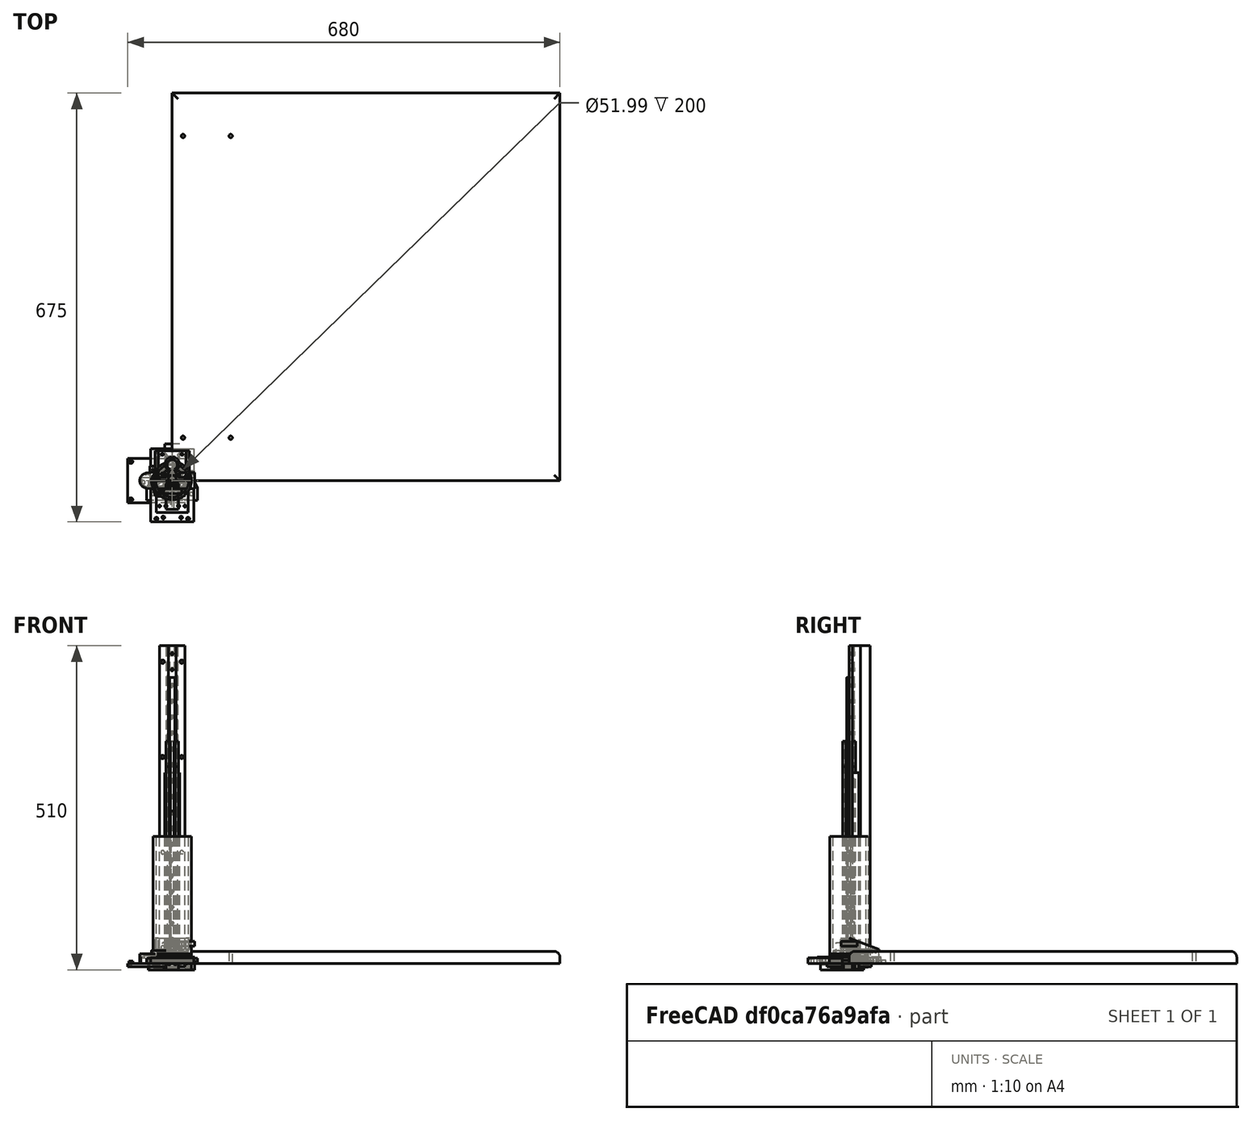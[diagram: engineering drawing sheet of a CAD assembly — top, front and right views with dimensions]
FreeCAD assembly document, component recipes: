
FREECAD ASSEMBLY — COMPONENT RECIPES ("MUSCLE_ROLLER_1V0")

This assembly document has 39 components, labeled P0..P38 below (a component is one placed body or linked part). 39 of them carry a construction recipe — the FreeCAD feature program that regenerates the part from scratch, quoted from this document or its linked companion documents; the rest are supplied as boundary geometry only. No exploded tour is included for this assembly.
NOTE — this tour is split across 2 documents so each fits a 32k-token context. This is document 1: the component sections continue in the remaining 1 document, each repeating the header above.
COMPONENT P0 — recipe-attached ("BAR_A_1V0", modeled in this document).
Construction recipe (the document's own serialized feature program — sketch geometry with constraints, then the solid features built on it; lengths are millimeters unless a unit is written):

FEATURE [Sketcher::SketchObject] Sketch100
  FullyConstrained = true
  MapMode = 5
  Support = -> [XY_Plane080]
  sketch-geometry (57):
    g0: LineSegment StartX=-10 StartY=10 StartZ=0 EndX=10 EndY=10 EndZ=0
    g1: LineSegment StartX=10 StartY=10 StartZ=0 EndX=10 EndY=-10 EndZ=0
    g2: LineSegment StartX=10 StartY=-10 StartZ=0 EndX=-10 EndY=-10 EndZ=0
    g3: LineSegment StartX=-10 StartY=-10 StartZ=0 EndX=-10 EndY=10 EndZ=0
    g4: LineSegment StartX=-3.9 StartY=-3.9 StartZ=0 EndX=3.9 EndY=-3.9 EndZ=0
    g5: LineSegment StartX=3.9 StartY=-3.9 StartZ=0 EndX=3.9 EndY=3.9 EndZ=0
    g6: LineSegment StartX=3.9 StartY=3.9 StartZ=0 EndX=-3.9 EndY=3.9 EndZ=0
    g7: LineSegment StartX=-3.9 StartY=3.9 StartZ=0 EndX=-3.9 EndY=-3.9 EndZ=0
    g8: LineSegment StartX=-8.2 StartY=8.2 StartZ=0 EndX=8.2 EndY=8.2 EndZ=0
    g9: LineSegment StartX=8.2 StartY=8.2 StartZ=0 EndX=8.2 EndY=-8.2 EndZ=0
    g10: LineSegment StartX=8.2 StartY=-8.2 StartZ=0 EndX=-8.2 EndY=-8.2 EndZ=0
    g11: LineSegment StartX=-8.2 StartY=-8.2 StartZ=0 EndX=-8.2 EndY=8.2 EndZ=0
    g12: Circle CenterX=0 CenterY=0 CenterZ=0 NormalX=0 NormalY=0 NormalZ=1 AngleXU=0 Radius=2.1
    g13: LineSegment StartX=-10 StartY=-10 StartZ=0 EndX=-10 EndY=-4.9 EndZ=0
    g14: LineSegment StartX=-10 StartY=-4.9 StartZ=0 EndX=-8.2 EndY=-3.1 EndZ=0
    g15: LineSegment StartX=-8.2 StartY=-3.1 StartZ=0 EndX=-8.2 EndY=-5.5 EndZ=0
    g16: LineSegment StartX=-6.56066 StartY=-5.5 StartZ=0 EndX=-3.9 EndY=-2.83934 EndZ=0
    g17: LineSegment StartX=-3.9 StartY=-2.83934 StartZ=0 EndX=-3.9 EndY=2.83934 EndZ=0
    g18: LineSegment StartX=-3.9 StartY=2.83934 StartZ=0 EndX=-6.56066 EndY=5.5 EndZ=0
    g19: LineSegment StartX=-8.2 StartY=5.5 StartZ=0 EndX=-8.2 EndY=3.1 EndZ=0
    g20: LineSegment StartX=-8.2 StartY=3.1 StartZ=0 EndX=-10 EndY=4.9 EndZ=0
    g21: LineSegment StartX=-10 StartY=4.9 StartZ=0 EndX=-10 EndY=10 EndZ=0
    g22: LineSegment StartX=-10 StartY=10 StartZ=0 EndX=-4.9 EndY=10 EndZ=0
    g23: LineSegment StartX=-4.9 StartY=10 StartZ=0 EndX=-3.1 EndY=8.2 EndZ=0
    g24: LineSegment StartX=-3.1 StartY=8.2 StartZ=0 EndX=-5.5 EndY=8.2 EndZ=0
    g25: LineSegment StartX=-5.5 StartY=6.56066 StartZ=0 EndX=-2.83934 EndY=3.9 EndZ=0
    g26: LineSegment StartX=-2.83934 StartY=3.9 StartZ=0 EndX=2.83934 EndY=3.9 EndZ=0
    g27: LineSegment StartX=2.83934 StartY=3.9 StartZ=0 EndX=5.5 EndY=6.56066 EndZ=0
    g28: LineSegment StartX=5.5 StartY=8.2 StartZ=0 EndX=3.1 EndY=8.2 EndZ=0
    g29: LineSegment StartX=3.1 StartY=8.2 StartZ=0 EndX=4.9 EndY=10 EndZ=0
    g30: LineSegment StartX=4.9 StartY=10 StartZ=0 EndX=10 EndY=10 EndZ=0
    g31: LineSegment StartX=10 StartY=10 StartZ=0 EndX=10 EndY=4.9 EndZ=0
    g32: LineSegment StartX=10 StartY=4.9 StartZ=0 EndX=8.2 EndY=3.1 EndZ=0
    g33: LineSegment StartX=8.2 StartY=3.1 StartZ=0 EndX=8.2 EndY=5.5 EndZ=0
    g34: LineSegment StartX=6.56066 StartY=5.5 StartZ=0 EndX=3.9 EndY=2.83934 EndZ=0
    g35: LineSegment StartX=3.9 StartY=2.83934 StartZ=0 EndX=3.9 EndY=-2.83934 EndZ=0
    g36: LineSegment StartX=3.9 StartY=-2.83934 StartZ=0 EndX=6.56066 EndY=-5.5 EndZ=0
    g37: LineSegment StartX=8.2 StartY=-5.5 StartZ=0 EndX=8.2 EndY=-3.1 EndZ=0
    g38: LineSegment StartX=8.2 StartY=-3.1 StartZ=0 EndX=10 EndY=-4.9 EndZ=0
    g39: LineSegment StartX=10 StartY=-4.9 StartZ=0 EndX=10 EndY=-10 EndZ=0
    g40: LineSegment StartX=10 StartY=-10 StartZ=0 EndX=4.9 EndY=-10 EndZ=0
    g41: LineSegment StartX=4.9 StartY=-10 StartZ=0 EndX=3.1 EndY=-8.2 EndZ=0
    g42: LineSegment StartX=3.1 StartY=-8.2 StartZ=0 EndX=5.5 EndY=-8.2 EndZ=0
    g43: LineSegment StartX=5.5 StartY=-6.56066 StartZ=0 EndX=2.83934 EndY=-3.9 EndZ=0
    g44: LineSegment StartX=2.83934 StartY=-3.9 StartZ=0 EndX=-2.83934 EndY=-3.9 EndZ=0
    g45: LineSegment StartX=-2.83934 StartY=-3.9 StartZ=0 EndX=-5.5 EndY=-6.56066 EndZ=0
    g46: LineSegment StartX=-5.5 StartY=-8.2 StartZ=0 EndX=-3.1 EndY=-8.2 EndZ=0
    g47: LineSegment StartX=-3.1 StartY=-8.2 StartZ=0 EndX=-4.9 EndY=-10 EndZ=0
    g48: LineSegment StartX=-4.9 StartY=-10 StartZ=0 EndX=-10 EndY=-10 EndZ=0
    g49: LineSegment StartX=-5.5 StartY=-8.2 StartZ=0 EndX=-5.5 EndY=-6.56066 EndZ=0
    g50: LineSegment StartX=-6.56066 StartY=-5.5 StartZ=0 EndX=-8.2 EndY=-5.5 EndZ=0
    g51: LineSegment StartX=-8.2 StartY=5.5 StartZ=0 EndX=-6.56066 EndY=5.5 EndZ=0
    g52: LineSegment StartX=-5.5 StartY=6.56066 StartZ=0 EndX=-5.5 EndY=8.2 EndZ=0
    g53: LineSegment StartX=5.5 StartY=8.2 StartZ=0 EndX=5.5 EndY=6.56066 EndZ=0
    g54: LineSegment StartX=6.56066 StartY=5.5 StartZ=0 EndX=8.2 EndY=5.5 EndZ=0
    g55: LineSegment StartX=6.56066 StartY=-5.5 StartZ=0 EndX=8.2 EndY=-5.5 EndZ=0
    g56: LineSegment StartX=5.5 StartY=-6.56066 StartZ=0 EndX=5.5 EndY=-8.2 EndZ=0
  constraints (133):
    c: Coincident(g0,g1)
    c: Coincident(g1,g2)
    c: Coincident(g2,g3)
    c: Coincident(g3,g0)
    c: Horizontal(g2)
    c: Vertical(g1)
    c: Equal(g3,g0)
    c: Symmetric(g0,g2,g-1)
    c: Symmetric(g0,g0,g-2)
    c: DistanceX(g0,g0) = 20
    c: Coincident(g4,g5)
    c: Coincident(g5,g6)
    c: Coincident(g6,g7)
    c: Coincident(g7,g4)
    c: Horizontal(g6)
    c: Vertical(g7)
    c: DistanceX(g2,g4) = 6.1
    c: DistanceY(g2,g4) = 6.1
    c: Coincident(g8,g9)
    c: Coincident(g9,g10)
    c: Coincident(g10,g11)
    c: Coincident(g11,g8)
    c: Horizontal(g8)
    c: Vertical(g11)
    c: DistanceX(g2,g10) = 1.8
    c: DistanceY(g2,g10) = 1.8
    c: Symmetric(g10,g9,g-2)
    c: Symmetric(g4,g4,g-2)
    c: Symmetric(g5,g4,g-1)
    c: Symmetric(g8,g9,g-1)
    c: Coincident(g12,g-1)
    c: Diameter(g12) = 4.2
    c: Coincident(g2,g13)
    c: PointOnObject(g13,g3)
    c: Coincident(g13,g14)
    c: PointOnObject(g14,g11)
    c: Coincident(g14,g15)
    c: PointOnObject(g16,g7)
    c: Coincident(g16,g17)
    c: Coincident(g17,g18)
    c: Coincident(g19,g20)
    c: Coincident(g20,g21)
    c: Coincident(g21,g0)
    c: Coincident(g21,g22)
    c: PointOnObject(g22,g0)
    c: Coincident(g22,g23)
    c: PointOnObject(g23,g8)
    c: Coincident(g23,g24)
    c: PointOnObject(g25,g6)
    c: Coincident(g25,g26)
    c: Coincident(g26,g27)
    c: Coincident(g28,g29)
    c: Coincident(g29,g30)
    c: Coincident(g30,g0)
    c: Coincident(g30,g31)
    c: Coincident(g31,g32)
    c: Coincident(g32,g33)
    c: Coincident(g34,g35)
    c: Coincident(g35,g36)
    c: Coincident(g37,g38)
    c: Coincident(g38,g39)
    c: Coincident(g39,g1)
    c: Coincident(g39,g40)
    c: PointOnObject(g40,g2)
    c: Coincident(g40,g41)
    c: Coincident(g41,g42)
    c: PointOnObject(g43,g4)
    c: Coincident(g43,g44)
    c: Coincident(g44,g45)
    c: Coincident(g46,g47)
    c: Coincident(g47,g48)
    c: Coincident(g48,g13)
    c: Angle(g2,g47) = 0.785398
    c: Parallel(g47,g45)
    c: Parallel(g45,g16)
    c: Parallel(g16,g14)
    c: DistanceY(g14,g19) = 6.2
    c: Symmetric(g19,g14,g-1)
    c: Equal(g48,g13)
    c: Coincident(g16,g50)
    c: Coincident(g15,g50)
    c: Coincident(g46,g49)
    c: Coincident(g45,g49)
    c: Vertical(g49)
    c: Horizontal(g50)
    c: Vertical(g52)
    c: Coincident(g24,g52)
    c: Coincident(g25,g52)
    c: Coincident(g18,g51)
    c: Coincident(g19,g51)
    c: DistanceY(g15,g19) = 11
    c: Symmetric(g20,g13,g-1)
    c: Equal(g50,g49)
    c: Equal(g46,g15)
    c: Horizontal(g46)
    c: Distance(g45,g16) = 1.5
    c: Symmetric(g15,g19,g-1)
    c: Equal(g22,g21)
    c: Symmetric(g23,g46,g-1)
    c: Symmetric(g25,g45,g-1)
    c: Symmetric(g18,g16,g-1)
    c: Symmetric(g17,g16,g-1)
    c: Symmetric(g25,g44,g-1)
    c: Symmetric(g23,g28,g-2)
    c: Symmetric(g29,g22,g-2)
    c: Symmetric(g26,g25,g-2)
    c: Coincident(g28,g53)
    c: Coincident(g27,g53)
    c: Coincident(g34,g54)
    c: Coincident(g33,g54)
    c: Symmetric(g28,g24,g-2)
    c: Symmetric(g27,g25,g-2)
    c: Symmetric(g34,g18,g-2)
    c: Symmetric(g33,g19,g-2)
    c: Symmetric(g34,g17,g-2)
    c: Horizontal(g28)
    c: Symmetric(g32,g37,g-1)
    c: Symmetric(g31,g38,g-1)
    c: Symmetric(g32,g19,g-2)
    c: Symmetric(g31,g20,g-2)
    c: Coincident(g36,g55)
    c: Coincident(g37,g55)
    c: Coincident(g42,g56)
    c: Coincident(g43,g56)
    c: Symmetric(g36,g34,g-1)
    c: Symmetric(g37,g33,g-1)
    c: Symmetric(g43,g45,g-2)
    c: Symmetric(g35,g34,g-1)
    c: Symmetric(g42,g46,g-2)
    c: Symmetric(g41,g46,g-2)
    c: Symmetric(g40,g47,g-2)
    c: Vertical(g37)
    c: Parallel(g43,g36)
FEATURE [PartDesign::Pad] Pad063
  Direction = (1,1,1)
  Length = 350
  Length2 = 100
  Profile = -> Sketch100
  Type = 0
FEATURE [PartDesign::Body] Body007
  Group = -> [Sketch100,Pad063]
  Origin = -> Origin079
  Tip = -> Pad063
COMPONENT P1 — recipe-attached ("BAR_B_1V0", modeled in this document).
Construction recipe (the document's own serialized feature program — sketch geometry with constraints, then the solid features built on it; lengths are millimeters unless a unit is written):

FEATURE [Sketcher::SketchObject] Sketch105
  FullyConstrained = true
  MapMode = 5
  Support = -> [XY_Plane086]
  sketch-geometry (57):
    g0: LineSegment StartX=-10 StartY=10 StartZ=0 EndX=10 EndY=10 EndZ=0
    g1: LineSegment StartX=10 StartY=10 StartZ=0 EndX=10 EndY=-10 EndZ=0
    g2: LineSegment StartX=10 StartY=-10 StartZ=0 EndX=-10 EndY=-10 EndZ=0
    g3: LineSegment StartX=-10 StartY=-10 StartZ=0 EndX=-10 EndY=10 EndZ=0
    g4: LineSegment StartX=-3.9 StartY=-3.9 StartZ=0 EndX=3.9 EndY=-3.9 EndZ=0
    g5: LineSegment StartX=3.9 StartY=-3.9 StartZ=0 EndX=3.9 EndY=3.9 EndZ=0
    g6: LineSegment StartX=3.9 StartY=3.9 StartZ=0 EndX=-3.9 EndY=3.9 EndZ=0
    g7: LineSegment StartX=-3.9 StartY=3.9 StartZ=0 EndX=-3.9 EndY=-3.9 EndZ=0
    g8: LineSegment StartX=-8.2 StartY=8.2 StartZ=0 EndX=8.2 EndY=8.2 EndZ=0
    g9: LineSegment StartX=8.2 StartY=8.2 StartZ=0 EndX=8.2 EndY=-8.2 EndZ=0
    g10: LineSegment StartX=8.2 StartY=-8.2 StartZ=0 EndX=-8.2 EndY=-8.2 EndZ=0
    g11: LineSegment StartX=-8.2 StartY=-8.2 StartZ=0 EndX=-8.2 EndY=8.2 EndZ=0
    g12: Circle CenterX=0 CenterY=0 CenterZ=0 NormalX=0 NormalY=0 NormalZ=1 AngleXU=0 Radius=2.1
    g13: LineSegment StartX=-10 StartY=-10 StartZ=0 EndX=-10 EndY=-4.9 EndZ=0
    g14: LineSegment StartX=-10 StartY=-4.9 StartZ=0 EndX=-8.2 EndY=-3.1 EndZ=0
    g15: LineSegment StartX=-8.2 StartY=-3.1 StartZ=0 EndX=-8.2 EndY=-5.5 EndZ=0
    g16: LineSegment StartX=-6.56066 StartY=-5.5 StartZ=0 EndX=-3.9 EndY=-2.83934 EndZ=0
    g17: LineSegment StartX=-3.9 StartY=-2.83934 StartZ=0 EndX=-3.9 EndY=2.83934 EndZ=0
    g18: LineSegment StartX=-3.9 StartY=2.83934 StartZ=0 EndX=-6.56066 EndY=5.5 EndZ=0
    g19: LineSegment StartX=-8.2 StartY=5.5 StartZ=0 EndX=-8.2 EndY=3.1 EndZ=0
    g20: LineSegment StartX=-8.2 StartY=3.1 StartZ=0 EndX=-10 EndY=4.9 EndZ=0
    g21: LineSegment StartX=-10 StartY=4.9 StartZ=0 EndX=-10 EndY=10 EndZ=0
    g22: LineSegment StartX=-10 StartY=10 StartZ=0 EndX=-4.9 EndY=10 EndZ=0
    g23: LineSegment StartX=-4.9 StartY=10 StartZ=0 EndX=-3.1 EndY=8.2 EndZ=0
    g24: LineSegment StartX=-3.1 StartY=8.2 StartZ=0 EndX=-5.5 EndY=8.2 EndZ=0
    g25: LineSegment StartX=-5.5 StartY=6.56066 StartZ=0 EndX=-2.83934 EndY=3.9 EndZ=0
    g26: LineSegment StartX=-2.83934 StartY=3.9 StartZ=0 EndX=2.83934 EndY=3.9 EndZ=0
    g27: LineSegment StartX=2.83934 StartY=3.9 StartZ=0 EndX=5.5 EndY=6.56066 EndZ=0
    g28: LineSegment StartX=5.5 StartY=8.2 StartZ=0 EndX=3.1 EndY=8.2 EndZ=0
    g29: LineSegment StartX=3.1 StartY=8.2 StartZ=0 EndX=4.9 EndY=10 EndZ=0
    g30: LineSegment StartX=4.9 StartY=10 StartZ=0 EndX=10 EndY=10 EndZ=0
    g31: LineSegment StartX=10 StartY=10 StartZ=0 EndX=10 EndY=4.9 EndZ=0
    g32: LineSegment StartX=10 StartY=4.9 StartZ=0 EndX=8.2 EndY=3.1 EndZ=0
    g33: LineSegment StartX=8.2 StartY=3.1 StartZ=0 EndX=8.2 EndY=5.5 EndZ=0
    g34: LineSegment StartX=6.56066 StartY=5.5 StartZ=0 EndX=3.9 EndY=2.83934 EndZ=0
    g35: LineSegment StartX=3.9 StartY=2.83934 StartZ=0 EndX=3.9 EndY=-2.83934 EndZ=0
    g36: LineSegment StartX=3.9 StartY=-2.83934 StartZ=0 EndX=6.56066 EndY=-5.5 EndZ=0
    g37: LineSegment StartX=8.2 StartY=-5.5 StartZ=0 EndX=8.2 EndY=-3.1 EndZ=0
    g38: LineSegment StartX=8.2 StartY=-3.1 StartZ=0 EndX=10 EndY=-4.9 EndZ=0
    g39: LineSegment StartX=10 StartY=-4.9 StartZ=0 EndX=10 EndY=-10 EndZ=0
    g40: LineSegment StartX=10 StartY=-10 StartZ=0 EndX=4.9 EndY=-10 EndZ=0
    g41: LineSegment StartX=4.9 StartY=-10 StartZ=0 EndX=3.1 EndY=-8.2 EndZ=0
    g42: LineSegment StartX=3.1 StartY=-8.2 StartZ=0 EndX=5.5 EndY=-8.2 EndZ=0
    g43: LineSegment StartX=5.5 StartY=-6.56066 StartZ=0 EndX=2.83934 EndY=-3.9 EndZ=0
    g44: LineSegment StartX=2.83934 StartY=-3.9 StartZ=0 EndX=-2.83934 EndY=-3.9 EndZ=0
    g45: LineSegment StartX=-2.83934 StartY=-3.9 StartZ=0 EndX=-5.5 EndY=-6.56066 EndZ=0
    g46: LineSegment StartX=-5.5 StartY=-8.2 StartZ=0 EndX=-3.1 EndY=-8.2 EndZ=0
    g47: LineSegment StartX=-3.1 StartY=-8.2 StartZ=0 EndX=-4.9 EndY=-10 EndZ=0
    g48: LineSegment StartX=-4.9 StartY=-10 StartZ=0 EndX=-10 EndY=-10 EndZ=0
    g49: LineSegment StartX=-5.5 StartY=-8.2 StartZ=0 EndX=-5.5 EndY=-6.56066 EndZ=0
    g50: LineSegment StartX=-6.56066 StartY=-5.5 StartZ=0 EndX=-8.2 EndY=-5.5 EndZ=0
    g51: LineSegment StartX=-8.2 StartY=5.5 StartZ=0 EndX=-6.56066 EndY=5.5 EndZ=0
    g52: LineSegment StartX=-5.5 StartY=6.56066 StartZ=0 EndX=-5.5 EndY=8.2 EndZ=0
    g53: LineSegment StartX=5.5 StartY=8.2 StartZ=0 EndX=5.5 EndY=6.56066 EndZ=0
    g54: LineSegment StartX=6.56066 StartY=5.5 StartZ=0 EndX=8.2 EndY=5.5 EndZ=0
    g55: LineSegment StartX=6.56066 StartY=-5.5 StartZ=0 EndX=8.2 EndY=-5.5 EndZ=0
    g56: LineSegment StartX=5.5 StartY=-6.56066 StartZ=0 EndX=5.5 EndY=-8.2 EndZ=0
  constraints (133):
    c: Coincident(g0,g1)
    c: Coincident(g1,g2)
    c: Coincident(g2,g3)
    c: Coincident(g3,g0)
    c: Horizontal(g2)
    c: Vertical(g1)
    c: Equal(g3,g0)
    c: Symmetric(g0,g2,g-1)
    c: Symmetric(g0,g0,g-2)
    c: DistanceX(g0,g0) = 20
    c: Coincident(g4,g5)
    c: Coincident(g5,g6)
    c: Coincident(g6,g7)
    c: Coincident(g7,g4)
    c: Horizontal(g6)
    c: Vertical(g7)
    c: DistanceX(g2,g4) = 6.1
    c: DistanceY(g2,g4) = 6.1
    c: Coincident(g8,g9)
    c: Coincident(g9,g10)
    c: Coincident(g10,g11)
    c: Coincident(g11,g8)
    c: Horizontal(g8)
    c: Vertical(g11)
    c: DistanceX(g2,g10) = 1.8
    c: DistanceY(g2,g10) = 1.8
    c: Symmetric(g10,g9,g-2)
    c: Symmetric(g4,g4,g-2)
    c: Symmetric(g5,g4,g-1)
    c: Symmetric(g8,g9,g-1)
    c: Coincident(g12,g-1)
    c: Diameter(g12) = 4.2
    c: Coincident(g2,g13)
    c: PointOnObject(g13,g3)
    c: Coincident(g13,g14)
    c: PointOnObject(g14,g11)
    c: Coincident(g14,g15)
    c: PointOnObject(g16,g7)
    c: Coincident(g16,g17)
    c: Coincident(g17,g18)
    c: Coincident(g19,g20)
    c: Coincident(g20,g21)
    c: Coincident(g21,g0)
    c: Coincident(g21,g22)
    c: PointOnObject(g22,g0)
    c: Coincident(g22,g23)
    c: PointOnObject(g23,g8)
    c: Coincident(g23,g24)
    c: PointOnObject(g25,g6)
    c: Coincident(g25,g26)
    c: Coincident(g26,g27)
    c: Coincident(g28,g29)
    c: Coincident(g29,g30)
    c: Coincident(g30,g0)
    c: Coincident(g30,g31)
    c: Coincident(g31,g32)
    c: Coincident(g32,g33)
    c: Coincident(g34,g35)
    c: Coincident(g35,g36)
    c: Coincident(g37,g38)
    c: Coincident(g38,g39)
    c: Coincident(g39,g1)
    c: Coincident(g39,g40)
    c: PointOnObject(g40,g2)
    c: Coincident(g40,g41)
    c: Coincident(g41,g42)
    c: PointOnObject(g43,g4)
    c: Coincident(g43,g44)
    c: Coincident(g44,g45)
    c: Coincident(g46,g47)
    c: Coincident(g47,g48)
    c: Coincident(g48,g13)
    c: Angle(g2,g47) = 0.785398
    c: Parallel(g47,g45)
    c: Parallel(g45,g16)
    c: Parallel(g16,g14)
    c: DistanceY(g14,g19) = 6.2
    c: Symmetric(g19,g14,g-1)
    c: Equal(g48,g13)
    c: Coincident(g16,g50)
    c: Coincident(g15,g50)
    c: Coincident(g46,g49)
    c: Coincident(g45,g49)
    c: Vertical(g49)
    c: Horizontal(g50)
    c: Vertical(g52)
    c: Coincident(g24,g52)
    c: Coincident(g25,g52)
    c: Coincident(g18,g51)
    c: Coincident(g19,g51)
    c: DistanceY(g15,g19) = 11
    c: Symmetric(g20,g13,g-1)
    c: Equal(g50,g49)
    c: Equal(g46,g15)
    c: Horizontal(g46)
    c: Distance(g45,g16) = 1.5
    c: Symmetric(g15,g19,g-1)
    c: Equal(g22,g21)
    c: Symmetric(g23,g46,g-1)
    c: Symmetric(g25,g45,g-1)
    c: Symmetric(g18,g16,g-1)
    c: Symmetric(g17,g16,g-1)
    c: Symmetric(g25,g44,g-1)
    c: Symmetric(g23,g28,g-2)
    c: Symmetric(g29,g22,g-2)
    c: Symmetric(g26,g25,g-2)
    c: Coincident(g28,g53)
    c: Coincident(g27,g53)
    c: Coincident(g34,g54)
    c: Coincident(g33,g54)
    c: Symmetric(g28,g24,g-2)
    c: Symmetric(g27,g25,g-2)
    c: Symmetric(g34,g18,g-2)
    c: Symmetric(g33,g19,g-2)
    c: Symmetric(g34,g17,g-2)
    c: Horizontal(g28)
    c: Symmetric(g32,g37,g-1)
    c: Symmetric(g31,g38,g-1)
    c: Symmetric(g32,g19,g-2)
    c: Symmetric(g31,g20,g-2)
    c: Coincident(g36,g55)
    c: Coincident(g37,g55)
    c: Coincident(g42,g56)
    c: Coincident(g43,g56)
    c: Symmetric(g36,g34,g-1)
    c: Symmetric(g37,g33,g-1)
    c: Symmetric(g43,g45,g-2)
    c: Symmetric(g35,g34,g-1)
    c: Symmetric(g42,g46,g-2)
    c: Symmetric(g41,g46,g-2)
    c: Symmetric(g40,g47,g-2)
    c: Vertical(g37)
    c: Parallel(g43,g36)
FEATURE [PartDesign::Pad] Pad066
  Direction = (1,1,1)
  Length = 310
  Length2 = 100
  Profile = -> Sketch105
  Type = 0
FEATURE [PartDesign::Body] Body008
  Group = -> [Sketch105,Pad066]
  Origin = -> Origin086
  Tip = -> Pad066
COMPONENT P2 — recipe-attached ("BASE_1V0", modeled in this document).
Construction recipe (the document's own serialized feature program — sketch geometry with constraints, then the solid features built on it; lengths are millimeters unless a unit is written):

FEATURE [PartDesign::CoordinateSystem] LCS_0064
  AttacherType = Attacher::AttachEngine3D
  MapMode = 2
  Support = -> [X_Axis070]
FEATURE [Sketcher::SketchObject] Sketch086
  FullyConstrained = true
  MapMode = 5
  Support = -> [XY_Plane070]
  sketch-geometry (10):
    g0: LineSegment StartX=0 StartY=0 StartZ=0 EndX=610 EndY=0 EndZ=0
    g1: LineSegment StartX=610 StartY=0 StartZ=0 EndX=610 EndY=610 EndZ=0
    g2: LineSegment StartX=610 StartY=610 StartZ=0 EndX=0 EndY=610 EndZ=0
    g3: LineSegment StartX=0 StartY=610 StartZ=0 EndX=0 EndY=0 EndZ=0
    g4: Circle CenterX=17 CenterY=67.5 CenterZ=0 NormalX=0 NormalY=0 NormalZ=1 AngleXU=0 Radius=2.75
    g5: Circle CenterX=92 CenterY=67.5 CenterZ=0 NormalX=0 NormalY=0 NormalZ=1 AngleXU=0 Radius=2.75
    g6: Circle CenterX=17 CenterY=542.5 CenterZ=0 NormalX=0 NormalY=0 NormalZ=1 AngleXU=0 Radius=2.75
    g7: Circle CenterX=92 CenterY=542.5 CenterZ=0 NormalX=0 NormalY=0 NormalZ=1 AngleXU=0 Radius=2.75
    g8: LineSegment StartX=17 StartY=542.5 StartZ=0 EndX=17 EndY=610 EndZ=0
    g9: LineSegment StartX=17 StartY=67.5 StartZ=0 EndX=17 EndY=0 EndZ=0
  constraints (29):
    c: Coincident(g0,g1)
    c: Coincident(g1,g2)
    c: Coincident(g2,g3)
    c: Coincident(g3,g0)
    c: Horizontal(g0)
    c: Horizontal(g2)
    c: Vertical(g1)
    c: Vertical(g3)
    c: DistanceX(g2,g2) = 610
    c: Coincident(g0,g-1)
    c: DistanceY(g3,g3) = 610
    c: Diameter(g6) = 5.5
    c: Equal(g6,g4)
    c: Equal(g6,g7)
    c: Equal(g6,g5)
    c: Horizontal(g4,g5)
    c: DistanceX(g4,g5) = 75
    c: DistanceX(g-1,g4) = 17
    c: Vertical(g5,g7)
    c: Horizontal(g7,g6)
    c: Vertical(g6,g4)
    c: Coincident(g8,g6)
    c: PointOnObject(g8,g2)
    c: Vertical(g8)
    c: Coincident(g9,g4)
    c: PointOnObject(g9,g0)
    c: Vertical(g9)
    c: Equal(g9,g8)
    c: DistanceY(g4,g6) = 475
FEATURE [PartDesign::Pad] Pad056
  Direction = (1,1,1)
  Length = 19
  Length2 = 100
  Profile = -> Sketch086
  Type = 0
FEATURE [PartDesign::Fillet] Fillet001
  Base = -> Pad056 [Edge4,Edge12,Edge10,Edge7]
  BaseFeature = -> Pad056
  Radius = 9
  SupportTransform = false
FEATURE [PartDesign::Body] Body_9
  Group = -> [LCS_0064,Sketch086,Pad056,Fillet001]
  Origin = -> Origin070
  Tip = -> Fillet001
COMPONENT P3 — recipe-attached ("BEARING_X_1V0", modeled in this document).
Construction recipe (the document's own serialized feature program — sketch geometry with constraints, then the solid features built on it; lengths are millimeters unless a unit is written):

FEATURE [PartDesign::CoordinateSystem] LCS_0092
  AttacherType = Attacher::AttachEngine3D
  MapMode = 2
  Support = -> [X_Axis100]
FEATURE [Sketcher::SketchObject] Sketch121
  FullyConstrained = true
  MapMode = 5
  Support = -> [XY_Plane100]
  sketch-geometry (9):
    g0: LineSegment StartX=-7 StartY=11 StartZ=0 EndX=-7 EndY=5 EndZ=0
    g1: LineSegment StartX=-7 StartY=5 StartZ=0 EndX=-17 EndY=5 EndZ=0
    g2: LineSegment StartX=-17 StartY=5 StartZ=0 EndX=-17 EndY=0 EndZ=0
    g3: LineSegment StartX=-17 StartY=0 StartZ=0 EndX=17 EndY=0 EndZ=0
    g4: LineSegment StartX=17 StartY=0 StartZ=0 EndX=17 EndY=5 EndZ=0
    g5: LineSegment StartX=17 StartY=5 StartZ=0 EndX=7 EndY=5 EndZ=0
    g6: LineSegment StartX=7 StartY=5 StartZ=0 EndX=7 EndY=11 EndZ=0
    g7: ArcOfCircle CenterX=0 CenterY=11 CenterZ=0 NormalX=0 NormalY=0 NormalZ=1 AngleXU=0 Radius=7 StartAngle=0 EndAngle=3.14159
    g8: Circle CenterX=0 CenterY=11 CenterZ=0 NormalX=0 NormalY=0 NormalZ=1 AngleXU=0 Radius=4.25
  constraints (27):
    c: Coincident(g0,g1)
    c: Horizontal(g1)
    c: Coincident(g1,g2)
    c: PointOnObject(g2,g-1)
    c: Vertical(g2)
    c: Coincident(g2,g3)
    c: PointOnObject(g3,g-1)
    c: Coincident(g3,g4)
    c: Coincident(g4,g5)
    c: Coincident(g5,g6)
    c: Vertical(g6)
    c: PointOnObject(g7,g-2)
    c: Coincident(g7,g0)
    c: Coincident(g7,g6)
    c: Horizontal(g5)
    c: DistanceY(g2,g2) = 5
    c: Coincident(g8,g7)
    c: Diameter(g8) = 8.5
    c: Diameter(g7) = 14
    c: Horizontal(g0,g7)
    c: Horizontal(g7,g6)
    c: Vertical(g0)
    c: Vertical(g4)
    c: Equal(g4,g2)
    c: DistanceX(g1,g1) = 10
    c: Equal(g5,g1)
    c: DistanceY(g-1,g7) = 11
FEATURE [PartDesign::Pad] Pad074
  Direction = (1,1,1)
  Length = 20
  Length2 = 100
  Midplane = true
  Profile = -> Sketch121
  Refine = true
  Type = 0
FEATURE [Sketcher::SketchObject] Sketch122
  FullyConstrained = true
  MapMode = 5
  Placement = pos=(0,0,0) rot=(1,0,0;1.5708rad)
  Support = -> [XZ_Plane099]
  sketch-geometry (2):
    g0: Circle CenterX=-12 CenterY=0 CenterZ=0 NormalX=0 NormalY=0 NormalZ=1 AngleXU=0 Radius=2.75
    g1: Circle CenterX=12 CenterY=0 CenterZ=0 NormalX=0 NormalY=0 NormalZ=1 AngleXU=0 Radius=2.75
  constraints (5):
    c: PointOnObject(g0,g-1)
    c: Diameter(g1) = 5.5
    c: Equal(g1,g0)
    c: Symmetric(g0,g1,g-2)
    c: DistanceX(g0,g1) = 24
FEATURE [PartDesign::Pocket] Pocket039
  BaseFeature = -> Pad074
  Length = 5
  Length2 = 100
  Profile = -> Sketch122
  Refine = true
  Type = 1
FEATURE [PartDesign::Body] Body_17
  Group = -> [LCS_0092,Sketch121,Pad074,Sketch122,Pocket039]
  Origin = -> Origin100
  Tip = -> Pocket039
COMPONENT P4 — recipe-attached ("CABLE_CARRIER", modeled in this document).
Construction recipe (the document's own serialized feature program — sketch geometry with constraints, then the solid features built on it; lengths are millimeters unless a unit is written):

FEATURE [PartDesign::CoordinateSystem] LCS_0120
  AttacherType = Attacher::AttachEngine3D
  MapMode = 2
  Support = -> [X_Axis130]
FEATURE [Sketcher::SketchObject] Sketch152
  FullyConstrained = true
  MapMode = 5
  Support = -> [XY_Plane130]
  sketch-geometry (4):
    g0: LineSegment StartX=-11.5 StartY=0 StartZ=0 EndX=11.5 EndY=0 EndZ=0
    g1: LineSegment StartX=11.5 StartY=0 StartZ=0 EndX=11.5 EndY=15 EndZ=0
    g2: LineSegment StartX=11.5 StartY=15 StartZ=0 EndX=-11.5 EndY=15 EndZ=0
    g3: LineSegment StartX=-11.5 StartY=15 StartZ=0 EndX=-11.5 EndY=0 EndZ=0
  constraints (11):
    c: Coincident(g0,g1)
    c: Coincident(g1,g2)
    c: Coincident(g2,g3)
    c: Coincident(g3,g0)
    c: Horizontal(g0)
    c: Vertical(g1)
    c: Vertical(g3)
    c: PointOnObject(g0,g-1)
    c: DistanceY(g1,g1) = 15
    c: DistanceX(g2,g2) = 23
    c: Symmetric(g2,g1,g-2)
FEATURE [PartDesign::Pad] Pad090
  Direction = (1,1,1)
  Length = 300
  Length2 = 100
  Profile = -> Sketch152
  Refine = true
  Type = 0
FEATURE [Sketcher::SketchObject] Sketch153
  FullyConstrained = true
  MapMode = 5
  Placement = pos=(0,0,0) rot=(1,0,0;1.5708rad)
  Support = -> [XZ_Plane129]
  sketch-geometry (3):
    g0: Circle CenterX=-5 CenterY=4 CenterZ=0 NormalX=0 NormalY=0 NormalZ=1 AngleXU=0 Radius=1.75
    g1: Circle CenterX=5 CenterY=4 CenterZ=0 NormalX=0 NormalY=0 NormalZ=1 AngleXU=0 Radius=1.75
    g2: Circle CenterX=0 CenterY=12 CenterZ=0 NormalX=0 NormalY=0 NormalZ=1 AngleXU=0 Radius=1.75
  constraints (8):
    c: PointOnObject(g2,g-2)
    c: Diameter(g0) = 3.5
    c: Equal(g0,g1)
    c: Equal(g0,g2)
    c: DistanceY(g0,g2) = 8
    c: Symmetric(g0,g1,g-2)
    c: DistanceX(g0,g1) = 10
    c: DistanceY(g-1,g1) = 4
FEATURE [PartDesign::Pocket] Pocket053
  BaseFeature = -> Pad090
  Length = 5
  Length2 = 100
  Profile = -> Sketch153
  Refine = true
  Type = 1
FEATURE [PartDesign::Body] Body_14
  Group = -> [LCS_0120,Sketch152,Pad090,Sketch153,Pocket053]
  Origin = -> Origin130
  Tip = -> Pocket053
COMPONENT P5 — recipe-attached ("LEAD_NUT_BRACK_X_1V0", modeled in this document).
Construction recipe (the document's own serialized feature program — sketch geometry with constraints, then the solid features built on it; lengths are millimeters unless a unit is written):

FEATURE [Sketcher::SketchObject] Sketch080
  FullyConstrained = true
  MapMode = 5
  Support = -> [XY_Plane066]
  sketch-geometry (29):
    g0: ArcOfCircle CenterX=0 CenterY=0 CenterZ=0 NormalX=0 NormalY=0 NormalZ=1 AngleXU=0 Radius=5.5 StartAngle=4.2508 EndAngle=5.17398
    g1: LineSegment StartX=-5.65685 StartY=5.65685 StartZ=0 EndX=5.65685 EndY=5.65685 EndZ=0
    g2: LineSegment StartX=5.65685 StartY=5.65685 StartZ=0 EndX=5.65685 EndY=-5.65685 EndZ=0
    g3: LineSegment StartX=5.65685 StartY=-5.65685 StartZ=0 EndX=-5.65685 EndY=-5.65685 EndZ=0
    g4: LineSegment StartX=-5.65685 StartY=-5.65685 StartZ=0 EndX=-5.65685 EndY=5.65685 EndZ=0
    g5: ArcOfCircle CenterX=-5.65685 CenterY=5.65685 CenterZ=0 NormalX=0 NormalY=0 NormalZ=1 AngleXU=0 Radius=1.75 StartAngle=0.785398 EndAngle=3.92699
    g6: ArcOfCircle CenterX=5.65685 CenterY=5.65685 CenterZ=0 NormalX=0 NormalY=0 NormalZ=1 AngleXU=0 Radius=1.75 StartAngle=5.49779 EndAngle=8.63938
    g7: ArcOfCircle CenterX=5.65685 CenterY=-5.65685 CenterZ=0 NormalX=0 NormalY=0 NormalZ=1 AngleXU=0 Radius=1.75 StartAngle=3.92699 EndAngle=7.06858
    g8: ArcOfCircle CenterX=-5.65685 CenterY=-5.65685 CenterZ=0 NormalX=0 NormalY=0 NormalZ=1 AngleXU=0 Radius=1.75 StartAngle=2.35619 EndAngle=5.49779
    g9: Circle CenterX=0 CenterY=0 CenterZ=0 NormalX=0 NormalY=0 NormalZ=1 AngleXU=0 Radius=8
    g10: LineSegment StartX=-6.89429 StartY=4.41942 StartZ=0 EndX=-4.92441 EndY=2.44953 EndZ=0
    g11: LineSegment StartX=6.89429 StartY=-4.41942 StartZ=0 EndX=4.92441 EndY=-2.44953 EndZ=0
    g12: LineSegment StartX=4.41942 StartY=6.89429 StartZ=0 EndX=2.44953 EndY=4.92441 EndZ=0
    g13: LineSegment StartX=-4.41942 StartY=-6.89429 StartZ=0 EndX=-2.44953 EndY=-4.92441 EndZ=0
    g14: ArcOfCircle CenterX=0 CenterY=0 CenterZ=0 NormalX=0 NormalY=0 NormalZ=1 AngleXU=0 Radius=5.5 StartAngle=2.68001 EndAngle=3.60318
    g15: ArcOfCircle CenterX=0 CenterY=0 CenterZ=0 NormalX=0 NormalY=0 NormalZ=1 AngleXU=0 Radius=5.5 StartAngle=1.10921 EndAngle=2.03238
    g16: ArcOfCircle CenterX=0 CenterY=0 CenterZ=0 NormalX=0 NormalY=0 NormalZ=1 AngleXU=0 Radius=5.5 StartAngle=5.8216 EndAngle=6.74477
    g17: LineSegment StartX=2.44953 StartY=-4.92441 StartZ=0 EndX=4.41942 EndY=-6.89429 EndZ=0
    g18: LineSegment StartX=4.92441 StartY=2.44953 StartZ=0 EndX=6.89429 EndY=4.41942 EndZ=0
    g19: LineSegment StartX=-2.44953 StartY=4.92441 StartZ=0 EndX=-4.41942 EndY=6.89429 EndZ=0
    g20: LineSegment StartX=-4.92441 StartY=-2.44953 StartZ=0 EndX=-6.89429 EndY=-4.41942 EndZ=0
    g21: LineSegment StartX=12 StartY=30 StartZ=0 EndX=12 EndY=-30 EndZ=0
    g22: LineSegment StartX=12 StartY=30 StartZ=0 EndX=2 EndY=30 EndZ=0
    g23: LineSegment StartX=2 StartY=-30 StartZ=0 EndX=12 EndY=-30 EndZ=0
    g24: ArcOfCircle CenterX=0 CenterY=0 CenterZ=0 NormalX=0 NormalY=0 NormalZ=1 AngleXU=0 Radius=15 StartAngle=1.5708 EndAngle=4.71239
    g25: LineSegment StartX=9e-16 StartY=15 StartZ=0 EndX=2 EndY=15 EndZ=0
    g26: LineSegment StartX=2 StartY=15 StartZ=0 EndX=2 EndY=30 EndZ=0
    g27: LineSegment StartX=-2.8e-15 StartY=-15 StartZ=0 EndX=2 EndY=-15 EndZ=0
    g28: LineSegment StartX=2 StartY=-15 StartZ=0 EndX=2 EndY=-30 EndZ=0
  constraints (74):
    c: Coincident(g0,g-1)
    c: Coincident(g1,g2)
    c: Coincident(g2,g3)
    c: Coincident(g3,g4)
    c: Coincident(g4,g1)
    c: Horizontal(g1)
    c: Horizontal(g3)
    c: Vertical(g2)
    c: Vertical(g4)
    c: Coincident(g5,g1)
    c: Coincident(g6,g1)
    c: Coincident(g7,g2)
    c: Coincident(g8,g3)
    c: Coincident(g9,g0)
    c: PointOnObject(g6,g9)
    c: Diameter(g9) = 16
    c: Diameter(g6) = 3.5
    c: Equal(g6,g5)
    c: Equal(g6,g8)
    c: Equal(g6,g7)
    c: PointOnObject(g5,g9)
    c: PointOnObject(g8,g9)
    c: Equal(g1,g4)
    c: Diameter(g0) = 11
    c: Tangent(g5,g10) = -1.5708
    c: Tangent(g8,g13) = -1.5708
    c: Tangent(g11,g7) = -1.5708
    c: PointOnObject(g14,g12)
    c: Equal(g0,g14)
    c: PointOnObject(g15,g11)
    c: Coincident(g0,g14)
    c: Equal(g0,g15)
    c: PointOnObject(g16,g13)
    c: Coincident(g0,g15)
    c: Equal(g0,g16)
    c: Coincident(g0,g16)
    c: Coincident(g17,g0)
    c: Tangent(g10,g17)
    c: Coincident(g13,g0)
    c: Tangent(g13,g18)
    c: Tangent(g11,g19)
    c: PointOnObject(g18,g16)
    c: Coincident(g11,g16)
    c: Coincident(g12,g15)
    c: Tangent(g12,g20)
    c: PointOnObject(g19,g15)
    c: Coincident(g10,g14)
    c: PointOnObject(g20,g14)
    c: Tangent(g6,g18) = -1.5708
    c: Tangent(g5,g19) = -1.5708
    c: Tangent(g8,g20) = -1.5708
    c: Tangent(g7,g17) = -1.5708
    c: Tangent(g6,g12) = -1.5708
    c: Symmetric(g21,g21,g-1)
    c: Coincident(g21,g22)
    c: Horizontal(g22)
    c: Coincident(g23,g21)
    c: Horizontal(g23)
    c: DistanceX(g-1,g21) = 12
    c: Coincident(g24,g0)
    c: PointOnObject(g24,g-2)
    c: PointOnObject(g24,g-2)
    c: Tangent(g24,g25) = 1.5708
    c: Coincident(g25,g26)
    c: Tangent(g24,g27) = -1.5708
    c: Coincident(g27,g28)
    c: DistanceY(g21,g21) = 60
    c: Vertical(g26)
    c: Vertical(g25,g27)
    c: Vertical(g28)
    c: Coincident(g23,g28)
    c: Coincident(g22,g26)
    c: Diameter(g24) = 30
    c: DistanceX(g22,g22) = 10
FEATURE [PartDesign::CoordinateSystem] LCS_0060
  AttacherType = Attacher::AttachEngine3D
  MapMode = 2
  Support = -> [X_Axis066]
FEATURE [PartDesign::Pad] Pad052
  Direction = (1,1,1)
  Length = 12
  Length2 = 100
  Midplane = true
  Profile = -> Sketch080
  Refine = true
  Type = 0
FEATURE [Sketcher::SketchObject] Sketch128
  FullyConstrained = true
  MapMode = 5
  Placement = pos=(0,0,0) rot=(0.57735,0.57735,0.57735;2.0944rad)
  Support = -> [YZ_Plane066]
  sketch-geometry (2):
    g0: Circle CenterX=-25 CenterY=0 CenterZ=0 NormalX=0 NormalY=0 NormalZ=1 AngleXU=0 Radius=1.75
    g1: Circle CenterX=25 CenterY=0 CenterZ=0 NormalX=0 NormalY=0 NormalZ=1 AngleXU=0 Radius=1.75
  constraints (5):
    c: PointOnObject(g0,g-1)
    c: Diameter(g0) = 3.5
    c: Equal(g0,g1)
    c: Symmetric(g0,g1,g-2)
    c: DistanceX(g0,g1) = 50
FEATURE [PartDesign::Pocket] Pocket044
  BaseFeature = -> Pad052
  Length = 5
  Length2 = 100
  Midplane = true
  Profile = -> Sketch128
  Refine = true
  Type = 1
FEATURE [PartDesign::Body] Body_021
  Group = -> [LCS_0060,Sketch080,Pad052,Sketch128,Pocket044]
  Origin = -> Origin066
  Tip = -> Pocket044
COMPONENT P6 — recipe-attached ("LEAD_NUT_BRACK_Z_1V0", modeled in this document).
Construction recipe (the document's own serialized feature program — sketch geometry with constraints, then the solid features built on it; lengths are millimeters unless a unit is written):

FEATURE [Sketcher::SketchObject] Sketch115
  FullyConstrained = true
  MapMode = 5
  Support = -> [XY_Plane093]
  sketch-geometry (25):
    g0: ArcOfCircle CenterX=0 CenterY=0 CenterZ=0 NormalX=0 NormalY=0 NormalZ=1 AngleXU=0 Radius=5.5 StartAngle=4.2508 EndAngle=5.17398
    g1: LineSegment StartX=-5.65685 StartY=5.65685 StartZ=0 EndX=5.65685 EndY=5.65685 EndZ=0
    g2: LineSegment StartX=5.65685 StartY=5.65685 StartZ=0 EndX=5.65685 EndY=-5.65685 EndZ=0
    g3: LineSegment StartX=5.65685 StartY=-5.65685 StartZ=0 EndX=-5.65685 EndY=-5.65685 EndZ=0
    g4: LineSegment StartX=-5.65685 StartY=-5.65685 StartZ=0 EndX=-5.65685 EndY=5.65685 EndZ=0
    g5: ArcOfCircle CenterX=-5.65685 CenterY=5.65685 CenterZ=0 NormalX=0 NormalY=0 NormalZ=1 AngleXU=0 Radius=1.75 StartAngle=0.785398 EndAngle=3.92699
    g6: ArcOfCircle CenterX=5.65685 CenterY=5.65685 CenterZ=0 NormalX=0 NormalY=0 NormalZ=1 AngleXU=0 Radius=1.75 StartAngle=5.49779 EndAngle=8.63938
    g7: ArcOfCircle CenterX=5.65685 CenterY=-5.65685 CenterZ=0 NormalX=0 NormalY=0 NormalZ=1 AngleXU=0 Radius=1.75 StartAngle=3.92699 EndAngle=7.06858
    g8: ArcOfCircle CenterX=-5.65685 CenterY=-5.65685 CenterZ=0 NormalX=0 NormalY=0 NormalZ=1 AngleXU=0 Radius=1.75 StartAngle=2.35619 EndAngle=5.49779
    g9: Circle CenterX=0 CenterY=0 CenterZ=0 NormalX=0 NormalY=0 NormalZ=1 AngleXU=0 Radius=8
    g10: LineSegment StartX=-6.89429 StartY=4.41942 StartZ=0 EndX=-4.92441 EndY=2.44953 EndZ=0
    g11: LineSegment StartX=6.89429 StartY=-4.41942 StartZ=0 EndX=4.92441 EndY=-2.44953 EndZ=0
    g12: LineSegment StartX=4.41942 StartY=6.89429 StartZ=0 EndX=2.44953 EndY=4.92441 EndZ=0
    g13: LineSegment StartX=-4.41942 StartY=-6.89429 StartZ=0 EndX=-2.44953 EndY=-4.92441 EndZ=0
    g14: ArcOfCircle CenterX=0 CenterY=0 CenterZ=0 NormalX=0 NormalY=0 NormalZ=1 AngleXU=0 Radius=5.5 StartAngle=2.68001 EndAngle=3.60318
    g15: ArcOfCircle CenterX=0 CenterY=0 CenterZ=0 NormalX=0 NormalY=0 NormalZ=1 AngleXU=0 Radius=5.5 StartAngle=1.10921 EndAngle=2.03238
    g16: ArcOfCircle CenterX=0 CenterY=0 CenterZ=0 NormalX=0 NormalY=0 NormalZ=1 AngleXU=0 Radius=5.5 StartAngle=5.8216 EndAngle=6.74477
    g17: LineSegment StartX=2.44953 StartY=-4.92441 StartZ=0 EndX=4.41942 EndY=-6.89429 EndZ=0
    g18: LineSegment StartX=4.92441 StartY=2.44953 StartZ=0 EndX=6.89429 EndY=4.41942 EndZ=0
    g19: LineSegment StartX=-2.44953 StartY=4.92441 StartZ=0 EndX=-4.41942 EndY=6.89429 EndZ=0
    g20: LineSegment StartX=-4.92441 StartY=-2.44953 StartZ=0 EndX=-6.89429 EndY=-4.41942 EndZ=0
    g21: LineSegment StartX=12 StartY=19 StartZ=0 EndX=12 EndY=-19 EndZ=0
    g22: LineSegment StartX=-12 StartY=19 StartZ=0 EndX=12 EndY=19 EndZ=0
    g23: LineSegment StartX=-12 StartY=-19 StartZ=0 EndX=12 EndY=-19 EndZ=0
    g24: LineSegment StartX=-12 StartY=19 StartZ=0 EndX=-12 EndY=-19 EndZ=0
  constraints (65):
    c: Coincident(g0,g-1)
    c: Coincident(g1,g2)
    c: Coincident(g2,g3)
    c: Coincident(g3,g4)
    c: Coincident(g4,g1)
    c: Horizontal(g1)
    c: Horizontal(g3)
    c: Vertical(g2)
    c: Vertical(g4)
    c: Coincident(g5,g1)
    c: Coincident(g6,g1)
    c: Coincident(g7,g2)
    c: Coincident(g8,g3)
    c: Coincident(g9,g0)
    c: PointOnObject(g6,g9)
    c: Diameter(g9) = 16
    c: Diameter(g6) = 3.5
    c: Equal(g6,g5)
    c: Equal(g6,g8)
    c: Equal(g6,g7)
    c: PointOnObject(g5,g9)
    c: PointOnObject(g8,g9)
    c: Equal(g1,g4)
    c: Diameter(g0) = 11
    c: Tangent(g5,g10) = -1.5708
    c: Tangent(g8,g13) = -1.5708
    c: Tangent(g11,g7) = -1.5708
    c: PointOnObject(g14,g12)
    c: Equal(g0,g14)
    c: PointOnObject(g15,g11)
    c: Coincident(g0,g14)
    c: Equal(g0,g15)
    c: PointOnObject(g16,g13)
    c: Coincident(g0,g15)
    c: Equal(g0,g16)
    c: Coincident(g0,g16)
    c: Coincident(g17,g0)
    c: Tangent(g10,g17)
    c: Coincident(g13,g0)
    c: Tangent(g13,g18)
    c: Tangent(g11,g19)
    c: PointOnObject(g18,g16)
    c: Coincident(g11,g16)
    c: Coincident(g12,g15)
    c: Tangent(g12,g20)
    c: PointOnObject(g19,g15)
    c: Coincident(g10,g14)
    c: PointOnObject(g20,g14)
    c: Tangent(g6,g18) = -1.5708
    c: Tangent(g5,g19) = -1.5708
    c: Tangent(g8,g20) = -1.5708
    c: Tangent(g7,g17) = -1.5708
    c: Tangent(g6,g12) = -1.5708
    c: Horizontal(g22)
    c: Coincident(g21,g23)
    c: Coincident(g21,g22)
    c: Symmetric(g21,g21,g-1)
    c: Horizontal(g23)
    c: DistanceX(g-1,g21) = 12
    c: Coincident(g24,g22)
    c: Coincident(g24,g23)
    c: Vertical(g24)
    c: DistanceX(g22,g-1) = 12
    c: DistanceY(g21,g21) = 38
    c: DistanceX(g7,g21) = 6.34315
FEATURE [PartDesign::Pad] Pad071
  Direction = (1,1,1)
  Length = 14
  Length2 = 100
  Midplane = true
  Profile = -> Sketch115
  Refine = true
  Type = 0
FEATURE [PartDesign::CoordinateSystem] LCS_0086
  AttacherType = Attacher::AttachEngine3D
  MapMode = 2
  Support = -> [X_Axis093]
FEATURE [Sketcher::SketchObject] Sketch117
  AttachmentOffset = pos=(0,0,12) rot=(0,0,1;0rad)
  FullyConstrained = true
  MapMode = 5
  Placement = pos=(12,-2.7e-15,2.7e-15) rot=(0.57735,0.57735,0.57735;2.0944rad)
  Support = -> [YZ_Plane093]
  sketch-geometry (2):
    g0: Circle CenterX=-14 CenterY=0 CenterZ=0 NormalX=0 NormalY=0 NormalZ=1 AngleXU=0 Radius=2.25
    g1: Circle CenterX=14 CenterY=0 CenterZ=0 NormalX=0 NormalY=0 NormalZ=1 AngleXU=0 Radius=2.25
  constraints (5):
    c: PointOnObject(g0,g-1)
    c: Diameter(g1) = 4.5
    c: Equal(g1,g0)
    c: Symmetric(g0,g1,g-2)
    c: DistanceX(g0,g1) = 28
FEATURE [PartDesign::Hole] Hole
  BaseFeature = -> Pad071
  Depth = 25
  DepthType = 0
  Diameter = 4.5
  DrillForDepth = false
  DrillPoint = 1
  DrillPointAngle = 118
  HoleCutCountersinkAngle = 90
  HoleCutCustomValues = false
  HoleCutDepth = 0
  HoleCutDiameter = 9
  HoleCutType = 7
  ModelActualThread = false
  Profile = -> Sketch117
  Refine = true
  Tapered = false
  TaperedAngle = 90
  ThreadAngle = 0
  ThreadClass = 0
  ThreadCutOffInner = 0
  ThreadCutOffOuter = 0
  ThreadDirection = 0
  ThreadFit = 0
  ThreadPitch = 0
  ThreadSize = 11
  ThreadType = 1
  Threaded = false
FEATURE [PartDesign::Body] Body_025
  Group = -> [LCS_0086,Sketch115,Pad071,Sketch117,Hole]
  Origin = -> Origin093
  Tip = -> Hole
COMPONENT P7 — recipe-attached ("CARRIAGE_PLATE_Z_1V0", modeled in this document).
Construction recipe (the document's own serialized feature program — sketch geometry with constraints, then the solid features built on it; lengths are millimeters unless a unit is written):

FEATURE [PartDesign::CoordinateSystem] LCS_0094
  AttacherType = Attacher::AttachEngine3D
  MapMode = 2
  Support = -> [X_Axis102]
FEATURE [Sketcher::SketchObject] Sketch123
  FullyConstrained = true
  MapMode = 5
  Support = -> [XY_Plane102]
  sketch-geometry (27):
    g0: LineSegment StartX=-34 StartY=50 StartZ=0 EndX=34 EndY=50 EndZ=0
    g1: LineSegment StartX=34 StartY=50 StartZ=0 EndX=34 EndY=-65 EndZ=0
    g2: LineSegment StartX=34 StartY=-65 StartZ=0 EndX=-34 EndY=-65 EndZ=0
    g3: LineSegment StartX=-34 StartY=-65 StartZ=0 EndX=-34 EndY=50 EndZ=0
    g4: LineSegment StartX=-10 StartY=35 StartZ=0 EndX=10 EndY=35 EndZ=0
    g5: LineSegment StartX=10 StartY=35 StartZ=0 EndX=10 EndY=15 EndZ=0
    g6: LineSegment StartX=10 StartY=15 StartZ=0 EndX=-10 EndY=15 EndZ=0
    g7: LineSegment StartX=-10 StartY=15 StartZ=0 EndX=-10 EndY=35 EndZ=0
    g8: LineSegment StartX=-10 StartY=-15 StartZ=0 EndX=10 EndY=-15 EndZ=0
    g9: LineSegment StartX=10 StartY=-15 StartZ=0 EndX=10 EndY=-35 EndZ=0
    g10: LineSegment StartX=10 StartY=-35 StartZ=0 EndX=-10 EndY=-35 EndZ=0
    g11: LineSegment StartX=-10 StartY=-35 StartZ=0 EndX=-10 EndY=-15 EndZ=0
    g12: Circle CenterX=-10 CenterY=35 CenterZ=0 NormalX=0 NormalY=0 NormalZ=1 AngleXU=0 Radius=1.9
    g13: Circle CenterX=10 CenterY=35 CenterZ=0 NormalX=0 NormalY=0 NormalZ=1 AngleXU=0 Radius=1.9
    g14: Circle CenterX=10 CenterY=15 CenterZ=0 NormalX=0 NormalY=0 NormalZ=1 AngleXU=0 Radius=1.9
    g15: Circle CenterX=-10 CenterY=15 CenterZ=0 NormalX=0 NormalY=0 NormalZ=1 AngleXU=0 Radius=1.9
    g16: Circle CenterX=-10 CenterY=-15 CenterZ=0 NormalX=0 NormalY=0 NormalZ=1 AngleXU=0 Radius=1.9
    g17: Circle CenterX=10 CenterY=-15 CenterZ=0 NormalX=0 NormalY=0 NormalZ=1 AngleXU=0 Radius=1.9
    g18: Circle CenterX=10 CenterY=-35 CenterZ=0 NormalX=0 NormalY=0 NormalZ=1 AngleXU=0 Radius=1.9
    g19: Circle CenterX=-10 CenterY=-35 CenterZ=0 NormalX=0 NormalY=0 NormalZ=1 AngleXU=0 Radius=1.9
    g20: LineSegment StartX=-14 StartY=50 StartZ=0 EndX=-14 EndY=-65 EndZ=0
    g21: Circle CenterX=-24 CenterY=40 CenterZ=0 NormalX=0 NormalY=0 NormalZ=1 AngleXU=0 Radius=2.75
    g22: Circle CenterX=-24 CenterY=11.65 CenterZ=0 NormalX=0 NormalY=0 NormalZ=1 AngleXU=0 Radius=2.75
    g23: Circle CenterX=24 CenterY=40 CenterZ=0 NormalX=0 NormalY=0 NormalZ=1 AngleXU=0 Radius=2.75
    g24: Circle CenterX=24 CenterY=11.65 CenterZ=0 NormalX=0 NormalY=0 NormalZ=1 AngleXU=0 Radius=2.75
    g25: Circle CenterX=-14 CenterY=-58 CenterZ=0 NormalX=0 NormalY=0 NormalZ=1 AngleXU=0 Radius=2.25
    g26: Circle CenterX=14 CenterY=-58 CenterZ=0 NormalX=0 NormalY=0 NormalZ=1 AngleXU=0 Radius=2.25
  constraints (68):
    c: Coincident(g0,g1)
    c: Coincident(g1,g2)
    c: Coincident(g2,g3)
    c: Coincident(g3,g0)
    c: Horizontal(g2)
    c: Vertical(g1)
    c: Coincident(g4,g5)
    c: Coincident(g5,g6)
    c: Coincident(g6,g7)
    c: Coincident(g7,g4)
    c: Horizontal(g4)
    c: Vertical(g5)
    c: Vertical(g7)
    c: Coincident(g8,g9)
    c: Coincident(g9,g10)
    c: Coincident(g10,g11)
    c: Coincident(g11,g8)
    c: Horizontal(g8)
    c: Horizontal(g10)
    c: Vertical(g9)
    c: Vertical(g11)
    c: Equal(g4,g7)
    c: Equal(g7,g8)
    c: Equal(g8,g11)
    c: DistanceY(g7,g7) = 20
    c: DistanceY(g8,g6) = 30
    c: Symmetric(g6,g8,g-1)
    c: Symmetric(g6,g5,g-2)
    c: Coincident(g12,g4)
    c: Coincident(g13,g4)
    c: Coincident(g14,g5)
    c: Coincident(g15,g6)
    c: Coincident(g16,g8)
    c: Coincident(g17,g8)
    c: Coincident(g18,g9)
    c: Coincident(g19,g10)
    c: Diameter(g19) = 3.8
    c: Equal(g19,g18)
    c: Equal(g19,g17)
    c: Equal(g19,g16)
    c: Equal(g19,g14)
    c: Equal(g19,g15)
    c: Equal(g19,g12)
    c: Equal(g19,g13)
    c: PointOnObject(g20,g0)
    c: PointOnObject(g20,g2)
    c: Vertical(g20)
    c: DistanceX(g20,g-1) = 14
    c: Diameter(g22) = 5.5
    c: Equal(g22,g21)
    c: DistanceY(g21,g0) = 10
    c: DistanceY(g22,g21) = 28.35
    c: Vertical(g21,g22)
    c: DistanceX(g21,g20) = 10
    c: Equal(g24,g23)
    c: Equal(g23,g21)
    c: Symmetric(g23,g21,g-2)
    c: Symmetric(g22,g24,g-2)
    c: DistanceX(g23,g0) = 10
    c: Symmetric(g0,g0,g-2)
    c: DistanceY(g-1,g0) = 50
    c: DistanceY(g2,g-1) = 65
    c: Vertical(g3)
    c: DistanceX(g25,g26) = 28
    c: Diameter(g25) = 4.5
    c: Equal(g25,g26)
    c: Symmetric(g25,g26,g-2)
    c: DistanceY(g1,g26) = 7
FEATURE [PartDesign::Pad] Pad075
  Direction = (1,1,1)
  Length = 9
  Length2 = 100
  Profile = -> Sketch123
  Refine = true
  Type = 0
FEATURE [Sketcher::SketchObject] Sketch145
  AttachmentOffset = pos=(0,0,9) rot=(0,0,1;0rad)
  FullyConstrained = true
  MapMode = 5
  Placement = pos=(0,0,9) rot=(0,0,1;0rad)
  Support = -> [XY_Plane102]
  sketch-geometry (2):
    g0: Circle CenterX=-25 CenterY=-60 CenterZ=0 NormalX=0 NormalY=0 NormalZ=1 AngleXU=0 Radius=2.5
    g1: Circle CenterX=25 CenterY=-60 CenterZ=0 NormalX=0 NormalY=0 NormalZ=1 AngleXU=0 Radius=2.5
  constraints (5):
    c: Symmetric(g1,g0,g-2)
    c: Diameter(g0) = 5
    c: Equal(g0,g1)
    c: DistanceY(g1,g-1) = 60
    c: DistanceX(g-1,g1) = 25
FEATURE [PartDesign::Pocket] Pocket050
  BaseFeature = -> Pad075
  Length = 2
  Length2 = 100
  Profile = -> Sketch145
  Refine = true
  Type = 0
FEATURE [PartDesign::Body] Body_18
  Group = -> [LCS_0094,Sketch123,Pad075,Sketch145,Pocket050]
  Origin = -> Origin102
  Tip = -> Pocket050
COMPONENT P8 — recipe-attached ("CARRIAGE_PLATE_X_1V0", modeled in this document).
Construction recipe (the document's own serialized feature program — sketch geometry with constraints, then the solid features built on it; lengths are millimeters unless a unit is written):

FEATURE [Sketcher::SketchObject] Sketch133
  FullyConstrained = true
  MapMode = 5
  Support = -> [XY_Plane110]
  sketch-geometry (31):
    g0: LineSegment StartX=-25 StartY=50 StartZ=0 EndX=25 EndY=50 EndZ=0
    g1: LineSegment StartX=25 StartY=50 StartZ=0 EndX=25 EndY=-50 EndZ=0
    g2: LineSegment StartX=25 StartY=-50 StartZ=0 EndX=-25 EndY=-50 EndZ=0
    g3: LineSegment StartX=-25 StartY=-50 StartZ=0 EndX=-25 EndY=50 EndZ=0
    g4: LineSegment StartX=-10 StartY=40 StartZ=0 EndX=10 EndY=40 EndZ=0
    g5: LineSegment StartX=10 StartY=40 StartZ=0 EndX=10 EndY=20 EndZ=0
    g6: LineSegment StartX=10 StartY=20 StartZ=0 EndX=-10 EndY=20 EndZ=0
    g7: LineSegment StartX=-10 StartY=20 StartZ=0 EndX=-10 EndY=40 EndZ=0
    g8: LineSegment StartX=-10 StartY=-20 StartZ=0 EndX=10 EndY=-20 EndZ=0
    g9: LineSegment StartX=10 StartY=-20 StartZ=0 EndX=10 EndY=-40 EndZ=0
    g10: LineSegment StartX=10 StartY=-40 StartZ=0 EndX=-10 EndY=-40 EndZ=0
    g11: LineSegment StartX=-10 StartY=-40 StartZ=0 EndX=-10 EndY=-20 EndZ=0
    g12: Circle CenterX=-10 CenterY=40 CenterZ=0 NormalX=0 NormalY=0 NormalZ=1 AngleXU=0 Radius=1.9
    g13: Circle CenterX=10 CenterY=40 CenterZ=0 NormalX=0 NormalY=0 NormalZ=1 AngleXU=0 Radius=1.9
    g14: Circle CenterX=10 CenterY=20 CenterZ=0 NormalX=0 NormalY=0 NormalZ=1 AngleXU=0 Radius=1.9
    g15: Circle CenterX=-10 CenterY=20 CenterZ=0 NormalX=0 NormalY=0 NormalZ=1 AngleXU=0 Radius=1.9
    g16: Circle CenterX=-10 CenterY=-20 CenterZ=0 NormalX=0 NormalY=0 NormalZ=1 AngleXU=0 Radius=1.9
    g17: Circle CenterX=10 CenterY=-20 CenterZ=0 NormalX=0 NormalY=0 NormalZ=1 AngleXU=0 Radius=1.9
    g18: Circle CenterX=10 CenterY=-40 CenterZ=0 NormalX=0 NormalY=0 NormalZ=1 AngleXU=0 Radius=1.9
    g19: Circle CenterX=-10 CenterY=-40 CenterZ=0 NormalX=0 NormalY=0 NormalZ=1 AngleXU=0 Radius=1.9
    g20: LineSegment StartX=-14 StartY=50 StartZ=0 EndX=-14 EndY=-50 EndZ=0
    g21: Circle CenterX=12.5 CenterY=0 CenterZ=0 NormalX=0 NormalY=0 NormalZ=1 AngleXU=0 Radius=1.75
    g22: Circle CenterX=-12.5 CenterY=0 CenterZ=0 NormalX=0 NormalY=0 NormalZ=1 AngleXU=0 Radius=1.75
    g23: Circle CenterX=20 CenterY=40 CenterZ=0 NormalX=0 NormalY=0 NormalZ=1 AngleXU=0 Radius=1.75
    g24: Circle CenterX=20 CenterY=20 CenterZ=0 NormalX=0 NormalY=0 NormalZ=1 AngleXU=0 Radius=1.75
    g25: Circle CenterX=-20 CenterY=40 CenterZ=0 NormalX=0 NormalY=0 NormalZ=1 AngleXU=0 Radius=1.75
    g26: Circle CenterX=-20 CenterY=20 CenterZ=0 NormalX=0 NormalY=0 NormalZ=1 AngleXU=0 Radius=1.75
    g27: Circle CenterX=-20 CenterY=-20 CenterZ=0 NormalX=0 NormalY=0 NormalZ=1 AngleXU=0 Radius=1.75
    g28: Circle CenterX=-20 CenterY=-40 CenterZ=0 NormalX=0 NormalY=0 NormalZ=1 AngleXU=0 Radius=1.75
    g29: Circle CenterX=20 CenterY=-20 CenterZ=0 NormalX=0 NormalY=0 NormalZ=1 AngleXU=0 Radius=1.75
    g30: Circle CenterX=20 CenterY=-40 CenterZ=0 NormalX=0 NormalY=0 NormalZ=1 AngleXU=0 Radius=1.75
  constraints (81):
    c: Coincident(g0,g1)
    c: Coincident(g1,g2)
    c: Coincident(g2,g3)
    c: Coincident(g3,g0)
    c: Horizontal(g2)
    c: Coincident(g4,g5)
    c: Coincident(g5,g6)
    c: Coincident(g6,g7)
    c: Coincident(g7,g4)
    c: Horizontal(g4)
    c: Vertical(g5)
    c: Vertical(g7)
    c: Coincident(g8,g9)
    c: Coincident(g9,g10)
    c: Coincident(g10,g11)
    c: Coincident(g11,g8)
    c: Horizontal(g8)
    c: Horizontal(g10)
    c: Vertical(g9)
    c: Vertical(g11)
    c: Equal(g4,g7)
    c: Equal(g7,g8)
    c: Equal(g8,g11)
    c: DistanceY(g7,g7) = 20
    c: DistanceY(g8,g6) = 40
    c: Symmetric(g6,g8,g-1)
    c: Symmetric(g6,g5,g-2)
    c: Coincident(g12,g4)
    c: Coincident(g13,g4)
    c: Coincident(g14,g5)
    c: Coincident(g15,g6)
    c: Coincident(g16,g8)
    c: Coincident(g17,g8)
    c: Coincident(g18,g9)
    c: Coincident(g19,g10)
    c: Diameter(g19) = 3.8
    c: Equal(g19,g18)
    c: Equal(g19,g17)
    c: Equal(g19,g16)
    c: Equal(g19,g14)
    c: Equal(g19,g15)
    c: Equal(g19,g12)
    c: Equal(g19,g13)
    c: PointOnObject(g20,g0)
    c: PointOnObject(g20,g2)
    c: Vertical(g20)
    c: DistanceX(g20,g-1) = 14
    c: Symmetric(g0,g0,g-2)
    c: Vertical(g3)
    c: PointOnObject(g21,g-1)
    c: Diameter(g22) = 3.5
    c: Equal(g22,g21)
    c: Symmetric(g22,g21,g-2)
    c: DistanceX(g22,g21) = 25
    c: DistanceX(g0,g0) = 50
    c: Symmetric(g0,g1,g-1)
    c: DistanceY(g1,g1) = 100
    c: Diameter(g30) = 3.5
    c: Equal(g30,g29)
    c: Equal(g30,g24)
    c: Equal(g30,g23)
    c: Diameter(g28) = 3.5
    c: Equal(g28,g27)
    c: Equal(g28,g26)
    c: Equal(g28,g25)
    c: Horizontal(g25,g12)
    c: Horizontal(g12,g23)
    c: Vertical(g23,g24)
    c: Vertical(g24,g29)
    c: Vertical(g29,g30)
    c: Horizontal(g24,g14)
    c: Horizontal(g14,g26)
    c: Horizontal(g29,g17)
    c: Horizontal(g17,g27)
    c: Horizontal(g30,g18)
    c: Horizontal(g18,g28)
    c: Vertical(g28,g27)
    c: Vertical(g27,g26)
    c: Vertical(g26,g25)
    c: DistanceX(g23,g0) = 5
    c: DistanceX(g0,g25) = 5
FEATURE [PartDesign::Pad] Pad079
  Direction = (1,1,1)
  Length = 10
  Length2 = 100
  Profile = -> Sketch133
  Refine = true
  Type = 0
FEATURE [PartDesign::CoordinateSystem] LCS_0102
  AttacherType = Attacher::AttachEngine3D
  MapMode = 2
  Support = -> [X_Axis109]
FEATURE [Sketcher::SketchObject] Sketch143
  AttachmentOffset = pos=(0,0,25) rot=(0,0,1;0rad)
  FullyConstrained = true
  MapMode = 5
  Placement = pos=(25,-5.6e-15,5.6e-15) rot=(0.57735,0.57735,0.57735;2.0944rad)
  Support = -> [YZ_Plane109]
  sketch-geometry (2):
    g0: Circle CenterX=-45 CenterY=5 CenterZ=0 NormalX=0 NormalY=0 NormalZ=1 AngleXU=0 Radius=2.5
    g1: Circle CenterX=45 CenterY=5 CenterZ=0 NormalX=0 NormalY=0 NormalZ=1 AngleXU=0 Radius=2.5
  constraints (5):
    c: DistanceY(g-1,g0) = 5
    c: Symmetric(g0,g1,g-2)
    c: DistanceX(g0,g1) = 90
    c: Diameter(g0) = 5
    c: Equal(g0,g1)
FEATURE [PartDesign::Pocket] Pocket049
  BaseFeature = -> Pad079
  Length = 2
  Length2 = 100
  Profile = -> Sketch143
  Refine = true
  Type = 0
FEATURE [Sketcher::SketchObject] Sketch149
  AttachmentOffset = pos=(0,0,-25) rot=(0,0,1;0rad)
  FullyConstrained = true
  MapMode = 5
  Placement = pos=(-25,5.6e-15,-5.6e-15) rot=(0.57735,0.57735,0.57735;2.0944rad)
  Support = -> [YZ_Plane109]
  sketch-geometry (2):
    g0: Circle CenterX=-10 CenterY=5 CenterZ=0 NormalX=0 NormalY=0 NormalZ=1 AngleXU=0 Radius=1.73
    g1: Circle CenterX=10 CenterY=5 CenterZ=0 NormalX=0 NormalY=0 NormalZ=1 AngleXU=0 Radius=1.73
  constraints (5):
    c: Diameter(g1) = 3.46
    c: Equal(g1,g0)
    c: Symmetric(g1,g0,g-2)
    c: DistanceY(g-1,g1) = 5
    c: DistanceX(g0,g1) = 20
FEATURE [PartDesign::Pocket] Pocket051
  BaseFeature = -> Pocket049
  Length = 10
  Length2 = 100
  Profile = -> Sketch149
  Refine = true
  Reversed = true
  Type = 0
FEATURE [PartDesign::Body] Body_028
  Group = -> [LCS_0102,Sketch133,Pad079,Sketch143,Pocket049,Sketch149,Pocket051]
  Origin = -> Origin109
  Tip = -> Pocket051
COMPONENT P9 — recipe-attached ("CARRIER_BRACK_A_1V0", modeled in this document).
Construction recipe (the document's own serialized feature program — sketch geometry with constraints, then the solid features built on it; lengths are millimeters unless a unit is written):

FEATURE [PartDesign::CoordinateSystem] LCS_0096
  AttacherType = Attacher::AttachEngine3D
  MapMode = 2
  Support = -> [X_Axis104]
FEATURE [Sketcher::SketchObject] Sketch129
  FullyConstrained = true
  MapMode = 5
  Support = -> [XY_Plane104]
  sketch-geometry (10):
    g0: LineSegment StartX=-10 StartY=12.5 StartZ=0 EndX=35 EndY=12.5 EndZ=0
    g1: LineSegment StartX=35 StartY=12.5 StartZ=0 EndX=35 EndY=-12.5 EndZ=0
    g2: LineSegment StartX=35 StartY=-12.5 StartZ=0 EndX=-10 EndY=-12.5 EndZ=0
    g3: LineSegment StartX=-10 StartY=-12.5 StartZ=0 EndX=-10 EndY=12.5 EndZ=0
    g4: Circle CenterX=0 CenterY=7.5 CenterZ=0 NormalX=0 NormalY=0 NormalZ=1 AngleXU=0 Radius=2.75
    g5: Circle CenterX=0 CenterY=-7.5 CenterZ=0 NormalX=0 NormalY=0 NormalZ=1 AngleXU=0 Radius=2.75
    g6: LineSegment StartX=10 StartY=12.5 StartZ=0 EndX=10 EndY=-12.5 EndZ=0
    g7: Circle CenterX=20 CenterY=5 CenterZ=0 NormalX=0 NormalY=0 NormalZ=1 AngleXU=0 Radius=1.75
    g8: Circle CenterX=20 CenterY=-5 CenterZ=0 NormalX=0 NormalY=0 NormalZ=1 AngleXU=0 Radius=1.75
    g9: Circle CenterX=28 CenterY=0 CenterZ=0 NormalX=0 NormalY=0 NormalZ=1 AngleXU=0 Radius=1.75
  constraints (28):
    c: Coincident(g0,g1)
    c: Coincident(g1,g2)
    c: Coincident(g2,g3)
    c: Coincident(g3,g0)
    c: Horizontal(g0)
    c: Horizontal(g2)
    c: Vertical(g1)
    c: PointOnObject(g4,g-2)
    c: Symmetric(g5,g4,g-1)
    c: DistanceY(g5,g4) = 15
    c: Diameter(g5) = 5.5
    c: Equal(g5,g4)
    c: DistanceX(g0,g-1) = 10
    c: DistanceY(g3,g3) = 25
    c: Symmetric(g0,g2,g-1)
    c: PointOnObject(g6,g0)
    c: PointOnObject(g6,g2)
    c: Vertical(g6)
    c: DistanceX(g-1,g6) = 10
    c: PointOnObject(g9,g-1)
    c: Diameter(g9) = 3.5
    c: Equal(g9,g8)
    c: Equal(g9,g7)
    c: Symmetric(g7,g8,g-1)
    c: DistanceY(g8,g7) = 10
    c: DistanceX(g6,g7) = 10
    c: DistanceX(g7,g9) = 8
    c: DistanceX(g-1,g0) = 35
FEATURE [PartDesign::Pad] Pad076
  Direction = (1,1,1)
  Length = 35
  Length2 = 100
  Profile = -> Sketch129
  Refine = true
  Type = 0
FEATURE [Sketcher::SketchObject] Sketch155
  FullyConstrained = true
  MapMode = 5
  Placement = pos=(0,0,0) rot=(1,0,0;1.5708rad)
  Support = -> [XZ_Plane103]
  sketch-geometry (8):
    g0: LineSegment StartX=-10 StartY=35 StartZ=0 EndX=5 EndY=35 EndZ=0
    g1: LineSegment StartX=5 StartY=35 StartZ=0 EndX=5 EndY=8 EndZ=0
    g2: LineSegment StartX=5 StartY=8 StartZ=0 EndX=-10 EndY=8 EndZ=0
    g3: LineSegment StartX=-10 StartY=8 StartZ=0 EndX=-10 EndY=35 EndZ=0
    g4: LineSegment StartX=35 StartY=27 StartZ=0 EndX=13 EndY=27 EndZ=0
    g5: LineSegment StartX=13 StartY=27 StartZ=0 EndX=13 EndY=0 EndZ=0
    g6: LineSegment StartX=13 StartY=0 StartZ=0 EndX=35 EndY=0 EndZ=0
    g7: LineSegment StartX=35 StartY=0 StartZ=0 EndX=35 EndY=27 EndZ=0
  constraints (24):
    c: Coincident(g0,g1)
    c: Coincident(g1,g2)
    c: Coincident(g2,g3)
    c: Coincident(g3,g0)
    c: Horizontal(g0)
    c: Horizontal(g2)
    c: Vertical(g1)
    c: Vertical(g3)
    c: Coincident(g4,g5)
    c: Coincident(g5,g6)
    c: Coincident(g6,g7)
    c: Coincident(g7,g4)
    c: Horizontal(g4)
    c: Horizontal(g6)
    c: Vertical(g5)
    c: Vertical(g7)
    c: PointOnObject(g5,g-1)
    c: DistanceX(g-1,g4) = 35
    c: DistanceY(g-1,g4) = 27
    c: DistanceX(g0,g-1) = 10
    c: DistanceY(g-1,g0) = 35
    c: DistanceX(g0,g4) = 8
    c: DistanceX(g0,g0) = 15
    c: DistanceY(g-1,g2) = 8
FEATURE [PartDesign::Pocket] Pocket055
  BaseFeature = -> Pad076
  Length = 5
  Length2 = 100
  Midplane = true
  Profile = -> Sketch155
  Refine = true
  Type = 1
FEATURE [PartDesign::Body] Body_19
  Group = -> [LCS_0096,Sketch129,Pad076,Sketch155,Pocket055]
  Origin = -> Origin104
  Tip = -> Pocket055
COMPONENT P10 — recipe-attached ("CARRIER_BRACK_B_1V0", modeled in this document).
Construction recipe (the document's own serialized feature program — sketch geometry with constraints, then the solid features built on it; lengths are millimeters unless a unit is written):

FEATURE [PartDesign::CoordinateSystem] LCS_0098
  AttacherType = Attacher::AttachEngine3D
  MapMode = 2
  Support = -> [X_Axis105]
FEATURE [Sketcher::SketchObject] Sketch130
  FullyConstrained = true
  MapMode = 5
  Support = -> [XY_Plane106]
  sketch-geometry (11):
    g0: Circle CenterX=-1e-16 CenterY=5 CenterZ=0 NormalX=0 NormalY=0 NormalZ=1 AngleXU=0 Radius=1.75
    g1: Circle CenterX=0 CenterY=-5 CenterZ=0 NormalX=0 NormalY=0 NormalZ=1 AngleXU=0 Radius=1.75
    g2: Circle CenterX=8 CenterY=0 CenterZ=0 NormalX=0 NormalY=0 NormalZ=1 AngleXU=0 Radius=1.75
    g3: Circle CenterX=-10 CenterY=-25 CenterZ=0 NormalX=0 NormalY=0 NormalZ=1 AngleXU=0 Radius=1.75
    g4: Circle CenterX=10 CenterY=-25 CenterZ=0 NormalX=0 NormalY=0 NormalZ=1 AngleXU=0 Radius=1.75
    g5: LineSegment StartX=-15 StartY=-30 StartZ=0 EndX=-15 EndY=-20 EndZ=0
    g6: LineSegment StartX=-15 StartY=-20 StartZ=0 EndX=-5 EndY=10 EndZ=0
    g7: LineSegment StartX=-5 StartY=10 StartZ=0 EndX=15 EndY=10 EndZ=0
    g8: LineSegment StartX=15 StartY=10 StartZ=0 EndX=15 EndY=-20 EndZ=0
    g9: LineSegment StartX=15 StartY=-20 StartZ=0 EndX=15 EndY=-30 EndZ=0
    g10: LineSegment StartX=15 StartY=-30 StartZ=0 EndX=-15 EndY=-30 EndZ=0
  constraints (30):
    c: PointOnObject(g2,g-1)
    c: Diameter(g2) = 3.5
    c: Equal(g2,g1)
    c: Equal(g2,g0)
    c: Symmetric(g0,g1,g-1)
    c: DistanceY(g1,g0) = 10
    c: DistanceX(g0,g2) = 8
    c: PointOnObject(g1,g-2)
    c: Diameter(g4) = 3.5
    c: Equal(g4,g3)
    c: Symmetric(g3,g4,g-2)
    c: DistanceX(g3,g4) = 20
    c: DistanceY(g4,g-1) = 25
    c: Coincident(g5,g6)
    c: Coincident(g6,g7)
    c: Horizontal(g7)
    c: Coincident(g7,g8)
    c: Coincident(g8,g9)
    c: Coincident(g9,g10)
    c: Coincident(g10,g5)
    c: DistanceX(g4,g9) = 5
    c: DistanceY(g9,g4) = 5
    c: Vertical(g9)
    c: Symmetric(g5,g9,g-2)
    c: DistanceY(g3,g5) = 5
    c: Symmetric(g5,g8,g-2)
    c: DistanceX(g6,g0) = 5
    c: DistanceY(g0,g6) = 5
    c: DistanceX(g2,g7) = 7
    c: Vertical(g8)
FEATURE [PartDesign::Pad] Pad077
  Direction = (1,1,1)
  Length = 33
  Length2 = 100
  Profile = -> Sketch130
  Refine = true
  Type = 0
FEATURE [Sketcher::SketchObject] Sketch154
  FullyConstrained = true
  MapMode = 5
  Placement = pos=(0,0,0) rot=(0.57735,0.57735,0.57735;2.0944rad)
  Support = -> [YZ_Plane105]
  sketch-geometry (8):
    g0: LineSegment StartX=-20 StartY=8 StartZ=0 EndX=-30 EndY=8 EndZ=0
    g1: LineSegment StartX=-30 StartY=8 StartZ=0 EndX=-30 EndY=33 EndZ=0
    g2: LineSegment StartX=-30 StartY=33 StartZ=0 EndX=-20 EndY=33 EndZ=0
    g3: LineSegment StartX=-20 StartY=33 StartZ=0 EndX=-20 EndY=8 EndZ=0
    g4: LineSegment StartX=10 StartY=25 StartZ=0 EndX=-12 EndY=25 EndZ=0
    g5: LineSegment StartX=-12 StartY=25 StartZ=0 EndX=-12 EndY=0 EndZ=0
    g6: LineSegment StartX=-12 StartY=0 StartZ=0 EndX=10 EndY=0 EndZ=0
    g7: LineSegment StartX=10 StartY=0 StartZ=0 EndX=10 EndY=25 EndZ=0
  constraints (24):
    c: Coincident(g0,g1)
    c: Coincident(g1,g2)
    c: Coincident(g2,g3)
    c: Coincident(g3,g0)
    c: Horizontal(g0)
    c: Horizontal(g2)
    c: Vertical(g1)
    c: Vertical(g3)
    c: Coincident(g4,g5)
    c: Coincident(g5,g6)
    c: Coincident(g6,g7)
    c: Coincident(g7,g4)
    c: Horizontal(g4)
    c: Horizontal(g6)
    c: Vertical(g5)
    c: Vertical(g7)
    c: PointOnObject(g6,g-1)
    c: DistanceY(g-1,g1) = 33
    c: DistanceX(g2,g4) = 8
    c: DistanceX(g-1,g4) = 10
    c: DistanceX(g4,g-1) = 12
    c: DistanceX(g2,g2) = 10
    c: DistanceY(g-1,g0) = 8
    c: DistanceY(g-1,g4) = 25
FEATURE [PartDesign::Pocket] Pocket054
  BaseFeature = -> Pad077
  Length = 5
  Length2 = 100
  Midplane = true
  Profile = -> Sketch154
  Refine = true
  Type = 1
FEATURE [PartDesign::Body] Body_026
  Group = -> [LCS_0098,Sketch130,Pad077,Sketch154,Pocket054]
  Origin = -> Origin105
  Tip = -> Pocket054
COMPONENT P11 — recipe-attached ("CARRIER_BRACK_C_1V0", modeled in this document).
Construction recipe (the document's own serialized feature program — sketch geometry with constraints, then the solid features built on it; lengths are millimeters unless a unit is written):

FEATURE [Sketcher::SketchObject] Sketch146
  FullyConstrained = true
  MapMode = 5
  Support = -> [XY_Plane123]
  sketch-geometry (10):
    g0: Circle CenterX=8 CenterY=-8 CenterZ=0 NormalX=0 NormalY=0 NormalZ=1 AngleXU=0 Radius=1.75
    g1: Circle CenterX=-10 CenterY=-25 CenterZ=0 NormalX=0 NormalY=0 NormalZ=1 AngleXU=0 Radius=1.75
    g2: Circle CenterX=10 CenterY=-25 CenterZ=0 NormalX=0 NormalY=0 NormalZ=1 AngleXU=0 Radius=1.75
    g3: LineSegment StartX=-15 StartY=-30 StartZ=0 EndX=-15 EndY=-20 EndZ=0
    g4: LineSegment StartX=-15 StartY=-20 StartZ=0 EndX=2 EndY=5 EndZ=0
    g5: LineSegment StartX=2 StartY=5 StartZ=0 EndX=24 EndY=5 EndZ=0
    g6: LineSegment StartX=24 StartY=5 StartZ=0 EndX=24 EndY=-30 EndZ=0
    g7: LineSegment StartX=24 StartY=-30 StartZ=0 EndX=-15 EndY=-30 EndZ=0
    g8: Circle CenterX=18 CenterY=-8 CenterZ=0 NormalX=0 NormalY=0 NormalZ=1 AngleXU=0 Radius=1.75
    g9: Circle CenterX=13 CenterY=0 CenterZ=0 NormalX=0 NormalY=0 NormalZ=1 AngleXU=0 Radius=1.75
  constraints (29):
    c: Diameter(g2) = 3.5
    c: Equal(g2,g1)
    c: Symmetric(g1,g2,g-2)
    c: DistanceX(g1,g2) = 20
    c: DistanceY(g2,g-1) = 25
    c: Coincident(g3,g4)
    c: Coincident(g4,g5)
    c: Horizontal(g5)
    c: Coincident(g5,g6)
    c: Coincident(g7,g3)
    c: DistanceY(g7,g2) = 5
    c: DistanceY(g1,g3) = 5
    c: Equal(g8,g9)
    c: Equal(g9,g0)
    c: Horizontal(g0,g8)
    c: DistanceX(g0,g8) = 10
    c: DistanceY(g0,g9) = 8
    c: DistanceX(g0,g9) = 5
    c: Diameter(g0) = 3.5
    c: PointOnObject(g9,g-1)
    c: DistanceY(g-1,g5) = 5
    c: DistanceX(g5,g5) = 22
    c: DistanceX(g9,g5) = 11
    c: DistanceX(g-1,g0) = 8
    c: Vertical(g3)
    c: DistanceX(g3,g1) = 5
    c: Coincident(g6,g7)
    c: Vertical(g6)
    c: Horizontal(g7)
FEATURE [PartDesign::Pad] Pad086
  Direction = (1,1,1)
  Length = 5
  Length2 = 100
  Profile = -> Sketch146
  Refine = true
  Type = 0
FEATURE [PartDesign::CoordinateSystem] LCS_0113
  AttacherType = Attacher::AttachEngine3D
  MapMode = 2
  Support = -> [X_Axis123]
FEATURE [PartDesign::Body] Body_030
  Group = -> [LCS_0113,Sketch146,Pad086]
  Origin = -> Origin123
  Tip = -> Pad086
COMPONENT P12 — recipe-attached ("CARRIER_BRACK_D_1V0", modeled in this document).
Construction recipe (the document's own serialized feature program — sketch geometry with constraints, then the solid features built on it; lengths are millimeters unless a unit is written):

FEATURE [PartDesign::CoordinateSystem] LCS_0116
  AttacherType = Attacher::AttachEngine3D
  MapMode = 2
  Support = -> [X_Axis126]
FEATURE [Sketcher::SketchObject] Sketch147
  FullyConstrained = true
  MapMode = 5
  Support = -> [XY_Plane126]
  sketch-geometry (6):
    g0: LineSegment StartX=-10 StartY=20 StartZ=0 EndX=10 EndY=20 EndZ=0
    g1: LineSegment StartX=10 StartY=20 StartZ=0 EndX=10 EndY=-20 EndZ=0
    g2: LineSegment StartX=10 StartY=-20 StartZ=0 EndX=-10 EndY=-20 EndZ=0
    g3: LineSegment StartX=-10 StartY=-20 StartZ=0 EndX=-10 EndY=20 EndZ=0
    g4: Circle CenterX=0 CenterY=10 CenterZ=0 NormalX=0 NormalY=0 NormalZ=1 AngleXU=0 Radius=2.75
    g5: Circle CenterX=0 CenterY=-10 CenterZ=0 NormalX=0 NormalY=0 NormalZ=1 AngleXU=0 Radius=2.75
  constraints (15):
    c: Coincident(g0,g1)
    c: Coincident(g1,g2)
    c: Coincident(g2,g3)
    c: Coincident(g3,g0)
    c: Horizontal(g2)
    c: Vertical(g3)
    c: Symmetric(g0,g0,g-2)
    c: DistanceX(g0,g0) = 20
    c: PointOnObject(g4,g-2)
    c: Diameter(g5) = 5.5
    c: Equal(g5,g4)
    c: DistanceY(g-1,g4) = 10
    c: Symmetric(g4,g5,g-1)
    c: DistanceY(g-1,g0) = 20
    c: Symmetric(g0,g1,g-1)
FEATURE [PartDesign::Pad] Pad087
  Direction = (1,1,1)
  Length = 5
  Length2 = 100
  Profile = -> Sketch147
  Refine = true
  Type = 0
FEATURE [Sketcher::SketchObject] Sketch148
  FullyConstrained = true
  MapMode = 5
  Placement = pos=(0,0,0) rot=(1,0,0;1.5708rad)
  Support = -> [XZ_Plane125]
  sketch-geometry (7):
    g0: LineSegment StartX=-10 StartY=0 StartZ=0 EndX=29 EndY=0 EndZ=0
    g1: LineSegment StartX=29 StartY=0 StartZ=0 EndX=29 EndY=33 EndZ=0
    g2: LineSegment StartX=29 StartY=33 StartZ=0 EndX=-10 EndY=33 EndZ=0
    g3: LineSegment StartX=-10 StartY=33 StartZ=0 EndX=-10 EndY=0 EndZ=0
    g4: Circle CenterX=14 CenterY=20 CenterZ=0 NormalX=0 NormalY=0 NormalZ=1 AngleXU=0 Radius=1.75
    g5: Circle CenterX=24 CenterY=20 CenterZ=0 NormalX=0 NormalY=0 NormalZ=1 AngleXU=0 Radius=1.75
    g6: Circle CenterX=19 CenterY=28 CenterZ=0 NormalX=0 NormalY=0 NormalZ=1 AngleXU=0 Radius=1.75
  constraints (21):
    c: Coincident(g0,g1)
    c: Coincident(g1,g2)
    c: Coincident(g2,g3)
    c: Coincident(g3,g0)
    c: Horizontal(g0)
    c: Horizontal(g2)
    c: Vertical(g1)
    c: Vertical(g3)
    c: PointOnObject(g0,g-1)
    c: DistanceX(g0,g-1) = 10
    c: Diameter(g6) = 3.5
    c: Equal(g6,g4)
    c: Equal(g6,g5)
    c: Horizontal(g4,g5)
    c: DistanceX(g4,g5) = 10
    c: DistanceY(g4,g6) = 8
    c: DistanceX(g4,g6) = 5
    c: DistanceX(g-1,g6) = 19
    c: DistanceX(g5,g1) = 5
    c: DistanceY(g-1,g5) = 20
    c: DistanceY(g6,g1) = 5
FEATURE [PartDesign::Pad] Pad088
  BaseFeature = -> Pad087
  Direction = (1,1,1)
  Length = 8
  Length2 = 100
  Midplane = true
  Profile = -> Sketch148
  Refine = true
  Type = 0
FEATURE [PartDesign::Body] Body_24
  Group = -> [LCS_0116,Sketch147,Pad087,Sketch148,Pad088]
  Origin = -> Origin126
  Tip = -> Pad088
COMPONENT P13 — recipe-attached ("COUPLER", modeled in this document).
Construction recipe (the document's own serialized feature program — sketch geometry with constraints, then the solid features built on it; lengths are millimeters unless a unit is written):

FEATURE [PartDesign::CoordinateSystem] LCS_0104
  AttacherType = Attacher::AttachEngine3D
  MapMode = 2
  Support = -> [X_Axis112]
FEATURE [Sketcher::SketchObject] Sketch134
  FullyConstrained = true
  MapMode = 5
  Support = -> [XY_Plane112]
  sketch-geometry (1):
    g0: Circle CenterX=0 CenterY=0 CenterZ=0 NormalX=0 NormalY=0 NormalZ=1 AngleXU=0 Radius=9.5
  constraints (2):
    c: Coincident(g0,g-1)
    c: Diameter(g0) = 19
FEATURE [PartDesign::Pad] Pad080
  Direction = (1,1,1)
  Length = 25
  Length2 = 100
  Profile = -> Sketch134
  Refine = true
  Type = 0
FEATURE [PartDesign::Body] Body_12
  Group = -> [LCS_0104,Sketch134,Pad080]
  Origin = -> Origin112
  Tip = -> Pad080
COMPONENT P14 — recipe-attached ("ENC_BRACK_X_1V0", modeled in this document).
Construction recipe (the document's own serialized feature program — sketch geometry with constraints, then the solid features built on it; lengths are millimeters unless a unit is written):

FEATURE [PartDesign::CoordinateSystem] LCS_0108
  AttacherType = Attacher::AttachEngine3D
  MapMode = 2
  Support = -> [X_Axis116]
FEATURE [Sketcher::SketchObject] Sketch140
  FullyConstrained = true
  MapMode = 5
  Support = -> [XY_Plane116]
  sketch-geometry (21):
    g0: LineSegment StartX=-28.7436 StartY=9.16717 StartZ=0 EndX=-10 EndY=25 EndZ=0
    g1: LineSegment StartX=-10 StartY=25 StartZ=0 EndX=10 EndY=25 EndZ=0
    g2: LineSegment StartX=10 StartY=25 StartZ=0 EndX=10 EndY=-25 EndZ=0
    g3: LineSegment StartX=10 StartY=-25 StartZ=0 EndX=-10 EndY=-25 EndZ=0
    g4: ArcOfCircle CenterX=-21 CenterY=0 CenterZ=0 NormalX=0 NormalY=0 NormalZ=1 AngleXU=0 Radius=12 StartAngle=2.27221 EndAngle=3.42342
    g5: Circle CenterX=-11 CenterY=0 CenterZ=0 NormalX=0 NormalY=0 NormalZ=1 AngleXU=0 Radius=1.3208
    g6: Circle CenterX=0 CenterY=15 CenterZ=0 NormalX=0 NormalY=0 NormalZ=1 AngleXU=0 Radius=2.75
    g7: Circle CenterX=0 CenterY=-15 CenterZ=0 NormalX=0 NormalY=0 NormalZ=1 AngleXU=0 Radius=2.75
    g8: LineSegment StartX=-7 StartY=3 StartZ=0 EndX=1 EndY=3 EndZ=0
    g9: LineSegment StartX=1 StartY=3 StartZ=0 EndX=1 EndY=-3 EndZ=0
    g10: LineSegment StartX=1 StartY=-3 StartZ=0 EndX=-7 EndY=-3 EndZ=0
    g11: LineSegment StartX=-7 StartY=-3 StartZ=0 EndX=-7 EndY=3 EndZ=0
    g12: Circle CenterX=-21 CenterY=-10 CenterZ=0 NormalX=0 NormalY=0 NormalZ=1 AngleXU=0 Radius=1.3208
    g13: LineSegment StartX=-24 StartY=-14 StartZ=0 EndX=-18 EndY=-14 EndZ=0
    g14: LineSegment StartX=-18 StartY=-14 StartZ=0 EndX=-18 EndY=-22 EndZ=0
    g15: LineSegment StartX=-18 StartY=-22 StartZ=0 EndX=-24 EndY=-22 EndZ=0
    g16: LineSegment StartX=-24 StartY=-22 StartZ=0 EndX=-24 EndY=-14 EndZ=0
    g17: LineSegment StartX=-21 StartY=0 StartZ=0 EndX=-21 EndY=-22 EndZ=0
    g18: LineSegment StartX=-10 StartY=-25 StartZ=0 EndX=-24 EndY=-25 EndZ=0
    g19: LineSegment StartX=-32.5266 StartY=-3.33728 StartZ=0 EndX=-26.8817 EndY=-22.8343 EndZ=0
    g20: ArcOfCircle CenterX=-24 CenterY=-22 CenterZ=0 NormalX=0 NormalY=0 NormalZ=1 AngleXU=0 Radius=3 StartAngle=3.42342 EndAngle=4.71239
  constraints (55):
    c: Coincident(g0,g1)
    c: Coincident(g1,g2)
    c: Coincident(g2,g3)
    c: Horizontal(g3)
    c: DistanceX(g1,g1) = 20
    c: Symmetric(g0,g1,g-2)
    c: Equal(g3,g1)
    c: Symmetric(g1,g2,g-1)
    c: PointOnObject(g4,g-1)
    c: Diameter(g4) = 24
    c: Tangent(g4,g0) = 1.5708
    c: PointOnObject(g5,g-1)
    c: Diameter(g5) = 2.6416
    c: DistanceX(g4,g5) = 10
    c: PointOnObject(g6,g-2)
    c: Diameter(g7) = 5.5
    c: Equal(g7,g6)
    c: Symmetric(g6,g7,g-1)
    c: DistanceY(g7,g6) = 30
    c: DistanceY(g2,g2) = 50
    c: Coincident(g8,g9)
    c: Coincident(g9,g10)
    c: Coincident(g10,g11)
    c: Coincident(g11,g8)
    c: Horizontal(g8)
    c: Horizontal(g10)
    c: Vertical(g9)
    c: DistanceX(g8,g8) = 8
    c: DistanceY(g11,g11) = 6
    c: Symmetric(g8,g10,g-1)
    c: DistanceX(g5,g8) = 12
    c: DistanceX(g4,g-1) = 21
    c: Vertical(g12,g4)
    c: Equal(g12,g5)
    c: DistanceY(g12,g4) = 10
    c: Coincident(g13,g14)
    c: Coincident(g14,g15)
    c: Coincident(g15,g16)
    c: Coincident(g16,g13)
    c: Horizontal(g13)
    c: Horizontal(g15)
    c: Vertical(g14)
    c: Vertical(g16)
    c: Equal(g13,g11)
    c: Equal(g14,g10)
    c: DistanceY(g14,g12) = 12
    c: Coincident(g17,g4)
    c: PointOnObject(g17,g15)
    c: Symmetric(g15,g14,g17)
    c: Coincident(g18,g3)
    c: Horizontal(g18)
    c: Tangent(g18,g20) = 1.5708
    c: Tangent(g19,g20) = -1.5708
    c: Coincident(g20,g15)
    c: Tangent(g19,g4) = -1.5708
FEATURE [PartDesign::Pad] Pad083
  Direction = (1,1,1)
  Length = 20
  Length2 = 100
  Profile = -> Sketch140
  Refine = true
  Type = 0
FEATURE [Sketcher::SketchObject] Sketch141
  FullyConstrained = true
  MapMode = 5
  Support = -> [XY_Plane116]
  sketch-geometry (9):
    g0: ArcOfCircle CenterX=-21 CenterY=0 CenterZ=0 NormalX=0 NormalY=0 NormalZ=1 AngleXU=0 Radius=9.25 StartAngle=0.359014 EndAngle=5.92417
    g1: LineSegment StartX=-12.3397 StartY=3.25 StartZ=0 EndX=1 EndY=3.25 EndZ=0
    g2: LineSegment StartX=1 StartY=3.25 StartZ=0 EndX=1 EndY=-3.25 EndZ=0
    g3: LineSegment StartX=1 StartY=-3.25 StartZ=0 EndX=-12.3397 EndY=-3.25 EndZ=0
    g4: LineSegment StartX=-17.75 StartY=-8.66025 StartZ=0 EndX=-17.75 EndY=-22 EndZ=0
    g5: LineSegment StartX=-17.75 StartY=-22 StartZ=0 EndX=-24.25 EndY=-22 EndZ=0
    g6: LineSegment StartX=-24.25 StartY=-22 StartZ=0 EndX=-24.25 EndY=-8.66025 EndZ=0
    g7: ArcOfCircle CenterX=-21 CenterY=0 CenterZ=0 NormalX=0 NormalY=0 NormalZ=1 AngleXU=0 Radius=9.25 StartAngle=5.0714 EndAngle=10.6366
    g8: LineSegment StartX=-21 StartY=0 StartZ=0 EndX=-21 EndY=-22 EndZ=0
  constraints (26):
    c: PointOnObject(g0,g-1)
    c: Diameter(g0) = 18.5
    c: DistanceX(g0,g-1) = 21
    c: Horizontal(g1)
    c: Coincident(g1,g2)
    c: Coincident(g2,g3)
    c: Horizontal(g3)
    c: DistanceY(g2,g2) = 6.5
    c: Symmetric(g1,g2,g-1)
    c: DistanceX(g0,g1) = 22
    c: Coincident(g0,g1)
    c: Coincident(g0,g3)
    c: PointOnObject(g4,g0)
    c: Vertical(g4)
    c: Coincident(g4,g5)
    c: Horizontal(g5)
    c: Coincident(g5,g6)
    c: Vertical(g6)
    c: Coincident(g7,g0)
    c: Coincident(g7,g6)
    c: Coincident(g7,g4)
    c: Equal(g5,g2)
    c: Coincident(g8,g7)
    c: Vertical(g8)
    c: Symmetric(g5,g4,g8)
    c: Equal(g4,g3)
FEATURE [PartDesign::Pocket] Pocket048
  BaseFeature = -> Pad083
  Length = 14
  Length2 = 100
  Profile = -> Sketch141
  Refine = true
  Reversed = true
  Type = 0
FEATURE [Sketcher::SketchObject] Sketch160
  FullyConstrained = true
  MapMode = 5
  Placement = pos=(0,0,0) rot=(1,0,0;1.5708rad)
  Support = -> [XZ_Plane115]
  sketch-geometry (4):
    g0: LineSegment StartX=-10 StartY=32 StartZ=0 EndX=10 EndY=32 EndZ=0
    g1: LineSegment StartX=10 StartY=32 StartZ=0 EndX=10 EndY=12 EndZ=0
    g2: LineSegment StartX=10 StartY=12 StartZ=0 EndX=-10 EndY=12 EndZ=0
    g3: LineSegment StartX=-10 StartY=12 StartZ=0 EndX=-10 EndY=32 EndZ=0
  constraints (11):
    c: Coincident(g0,g1)
    c: Coincident(g1,g2)
    c: Coincident(g2,g3)
    c: Coincident(g3,g0)
    c: Horizontal(g0)
    c: Vertical(g1)
    c: Vertical(g3)
    c: Equal(g0,g3)
    c: DistanceX(g0,g0) = 20
    c: Symmetric(g2,g1,g-2)
    c: DistanceY(g-1,g1) = 12
FEATURE [PartDesign::Pocket] Pocket059
  BaseFeature = -> Pocket048
  Length = 5
  Length2 = 100
  Midplane = true
  Profile = -> Sketch160
  Refine = true
  Type = 1
FEATURE [PartDesign::Body] Body_21
  Group = -> [LCS_0108,Sketch140,Pad083,Sketch141,Pocket048,Sketch160,Pocket059]
  Origin = -> Origin116
  Tip = -> Pocket059
COMPONENT P15 — recipe-attached ("ENC_BRACK_Z_1V0", modeled in this document).
Construction recipe (the document's own serialized feature program — sketch geometry with constraints, then the solid features built on it; lengths are millimeters unless a unit is written):

FEATURE [PartDesign::CoordinateSystem] LCS_0117
  AttacherType = Attacher::AttachEngine3D
  MapMode = 2
  Support = -> [X_Axis127]
FEATURE [Sketcher::SketchObject] Sketch150
  FullyConstrained = true
  MapMode = 5
  Support = -> [XY_Plane128]
  sketch-geometry (13):
    g0: LineSegment StartX=-40.0389 StartY=11.9549 StartZ=0 EndX=-5 EndY=15 EndZ=0
    g1: LineSegment StartX=-5 StartY=15 StartZ=0 EndX=5 EndY=15 EndZ=0
    g2: LineSegment StartX=5 StartY=15 StartZ=0 EndX=5 EndY=-15 EndZ=0
    g3: LineSegment StartX=5 StartY=-15 StartZ=0 EndX=-5 EndY=-15 EndZ=0
    g4: LineSegment StartX=-5 StartY=-15 StartZ=0 EndX=-40.0389 EndY=-11.9549 EndZ=0
    g5: ArcOfCircle CenterX=-39 CenterY=0 CenterZ=0 NormalX=0 NormalY=0 NormalZ=1 AngleXU=0 Radius=12 StartAngle=1.65748 EndAngle=4.6257
    g6: Circle CenterX=-29 CenterY=0 CenterZ=0 NormalX=0 NormalY=0 NormalZ=1 AngleXU=0 Radius=1.3208
    g7: Circle CenterX=0 CenterY=10 CenterZ=0 NormalX=0 NormalY=0 NormalZ=1 AngleXU=0 Radius=2.5
    g8: Circle CenterX=0 CenterY=-10 CenterZ=0 NormalX=0 NormalY=0 NormalZ=1 AngleXU=0 Radius=2.5
    g9: LineSegment StartX=-25 StartY=3 StartZ=0 EndX=-17 EndY=3 EndZ=0
    g10: LineSegment StartX=-17 StartY=3 StartZ=0 EndX=-17 EndY=-3 EndZ=0
    g11: LineSegment StartX=-17 StartY=-3 StartZ=0 EndX=-25 EndY=-3 EndZ=0
    g12: LineSegment StartX=-25 StartY=-3 StartZ=0 EndX=-25 EndY=3 EndZ=0
  constraints (34):
    c: Coincident(g0,g1)
    c: Coincident(g1,g2)
    c: Coincident(g2,g3)
    c: Horizontal(g3)
    c: Coincident(g3,g4)
    c: Symmetric(g0,g1,g-2)
    c: Equal(g3,g1)
    c: Symmetric(g1,g2,g-1)
    c: PointOnObject(g5,g-1)
    c: Diameter(g5) = 24
    c: Tangent(g5,g0) = 1.5708
    c: Tangent(g5,g4) = 1.5708
    c: PointOnObject(g6,g-1)
    c: Diameter(g6) = 2.6416
    c: DistanceX(g5,g6) = 10
    c: PointOnObject(g7,g-2)
    c: Diameter(g8) = 5
    c: Equal(g8,g7)
    c: Symmetric(g7,g8,g-1)
    c: DistanceY(g8,g7) = 20
    c: DistanceY(g2,g2) = 30
    c: Coincident(g9,g10)
    c: Coincident(g10,g11)
    c: Coincident(g11,g12)
    c: Coincident(g12,g9)
    c: Horizontal(g9)
    c: Horizontal(g11)
    c: Vertical(g10)
    c: DistanceX(g9,g9) = 8
    c: DistanceY(g12,g12) = 6
    c: Symmetric(g9,g11,g-1)
    c: DistanceX(g6,g9) = 12
    c: DistanceX(g5,g-1) = 39
    c: DistanceX(g-1,g1) = 5
FEATURE [PartDesign::Pad] Pad089
  Direction = (1,1,1)
  Length = 15
  Length2 = 100
  Profile = -> Sketch150
  Refine = true
  Type = 0
FEATURE [Sketcher::SketchObject] Sketch151
  FullyConstrained = true
  MapMode = 5
  Support = -> [XY_Plane128]
  sketch-geometry (4):
    g0: ArcOfCircle CenterX=-39 CenterY=0 CenterZ=0 NormalX=0 NormalY=0 NormalZ=1 AngleXU=0 Radius=9.25 StartAngle=0.359014 EndAngle=5.92417
    g1: LineSegment StartX=-30.3397 StartY=3.25 StartZ=0 EndX=-17 EndY=3.25 EndZ=0
    g2: LineSegment StartX=-17 StartY=3.25 StartZ=0 EndX=-17 EndY=-3.25 EndZ=0
    g3: LineSegment StartX=-17 StartY=-3.25 StartZ=0 EndX=-30.3397 EndY=-3.25 EndZ=0
  constraints (12):
    c: PointOnObject(g0,g-1)
    c: Diameter(g0) = 18.5
    c: DistanceX(g0,g-1) = 39
    c: Horizontal(g1)
    c: Coincident(g1,g2)
    c: Coincident(g2,g3)
    c: Horizontal(g3)
    c: DistanceY(g2,g2) = 6.5
    c: Symmetric(g1,g2,g-1)
    c: DistanceX(g0,g1) = 22
    c: Coincident(g0,g1)
    c: Coincident(g0,g3)
FEATURE [PartDesign::Pocket] Pocket052
  BaseFeature = -> Pad089
  Length = 12
  Length2 = 100
  Profile = -> Sketch151
  Refine = true
  Reversed = true
  Type = 0
FEATURE [PartDesign::Body] Body_031
  Group = -> [LCS_0117,Sketch150,Pad089,Sketch151,Pocket052]
  Origin = -> Origin128
  Tip = -> Pocket052
COMPONENT P16 — recipe-attached ("ENC_PCB_1V0", modeled in this document).
Construction recipe (the document's own serialized feature program — sketch geometry with constraints, then the solid features built on it; lengths are millimeters unless a unit is written):

FEATURE [Sketcher::SketchObject] Sketch107
  FullyConstrained = true
  MapMode = 5
  Support = -> [XY_Plane117]
  sketch-geometry (5):
    g0: LineSegment StartX=-3 StartY=-21 StartZ=0 EndX=3 EndY=-21 EndZ=0
    g1: LineSegment StartX=3 StartY=-21 StartZ=0 EndX=3 EndY=4 EndZ=0
    g2: LineSegment StartX=3 StartY=4 StartZ=0 EndX=-3 EndY=4 EndZ=0
    g3: LineSegment StartX=-3 StartY=4 StartZ=0 EndX=-3 EndY=-21 EndZ=0
    g4: Circle CenterX=0 CenterY=-10 CenterZ=0 NormalX=0 NormalY=0 NormalZ=1 AngleXU=0 Radius=1.75
  constraints (14):
    c: Coincident(g0,g1)
    c: Coincident(g1,g2)
    c: Coincident(g2,g3)
    c: Coincident(g3,g0)
    c: Horizontal(g0)
    c: Vertical(g1)
    c: Vertical(g3)
    c: Symmetric(g1,g2,g-2)
    c: DistanceY(g3,g3) = 25
    c: DistanceY(g-1,g2) = 4
    c: DistanceX(g2,g2) = 6
    c: PointOnObject(g4,g-2)
    c: Diameter(g4) = 3.5
    c: DistanceY(g4,g1) = 14
FEATURE [PartDesign::Pad] Pad082
  Direction = (1,1,1)
  Length = 1.6
  Length2 = 100
  Profile = -> Sketch107
  Type = 0
FEATURE [PartDesign::CoordinateSystem] LCS_0023
  AttacherType = Attacher::AttachEngine3D
  MapMode = 2
  Support = -> [X_Axis118]
FEATURE [PartDesign::Body] Body_029
  Group = -> [LCS_0023,Sketch107,Pad082]
  Origin = -> Origin118
  Tip = -> Pad082
COMPONENT P17 — recipe-attached ("END_CAP_1V0", modeled in this document).
Construction recipe (the document's own serialized feature program — sketch geometry with constraints, then the solid features built on it; lengths are millimeters unless a unit is written):

FEATURE [PartDesign::CoordinateSystem] LCS_0122
  AttacherType = Attacher::AttachEngine3D
  MapMode = 2
  Support = -> [X_Axis132]
FEATURE [Sketcher::SketchObject] Sketch156
  FullyConstrained = true
  MapMode = 5
  Support = -> [XY_Plane132]
  sketch-geometry (12):
    g0: LineSegment StartX=-10 StartY=12 StartZ=0 EndX=10 EndY=12 EndZ=0
    g1: LineSegment StartX=12 StartY=10 StartZ=0 EndX=12 EndY=-10 EndZ=0
    g2: LineSegment StartX=10 StartY=-12 StartZ=0 EndX=-10 EndY=-12 EndZ=0
    g3: LineSegment StartX=-12 StartY=-10 StartZ=0 EndX=-12 EndY=10 EndZ=0
    g4: ArcOfCircle CenterX=-10 CenterY=10 CenterZ=0 NormalX=0 NormalY=0 NormalZ=1 AngleXU=0 Radius=2 StartAngle=1.5708 EndAngle=3.14159
    g5: ArcOfCircle CenterX=10 CenterY=10 CenterZ=0 NormalX=0 NormalY=0 NormalZ=1 AngleXU=0 Radius=2 StartAngle=-9e-16 EndAngle=1.5708
    g6: ArcOfCircle CenterX=10 CenterY=-10 CenterZ=0 NormalX=0 NormalY=0 NormalZ=1 AngleXU=0 Radius=2 StartAngle=4.71239 EndAngle=6.28319
    g7: ArcOfCircle CenterX=-10 CenterY=-10 CenterZ=0 NormalX=0 NormalY=0 NormalZ=1 AngleXU=0 Radius=2 StartAngle=3.14159 EndAngle=4.71239
    g8: LineSegment StartX=-10 StartY=10 StartZ=0 EndX=10 EndY=10 EndZ=0
    g9: LineSegment StartX=10 StartY=10 StartZ=0 EndX=10 EndY=-10 EndZ=0
    g10: LineSegment StartX=10 StartY=-10 StartZ=0 EndX=-10 EndY=-10 EndZ=0
    g11: LineSegment StartX=-10 StartY=-10 StartZ=0 EndX=-10 EndY=10 EndZ=0
  constraints (27):
    c: Horizontal(g0)
    c: Horizontal(g2)
    c: Vertical(g1)
    c: Vertical(g3)
    c: Tangent(g0,g4) = 1.5708
    c: Tangent(g3,g4) = 1.5708
    c: Tangent(g0,g5) = 1.5708
    c: Tangent(g1,g5) = 1.5708
    c: Tangent(g1,g6) = 1.5708
    c: Tangent(g2,g6) = 1.5708
    c: Tangent(g2,g7) = 1.5708
    c: Tangent(g3,g7) = 1.5708
    c: Diameter(g4) = 4
    c: Equal(g4,g5)
    c: Coincident(g8,g9)
    c: Coincident(g9,g10)
    c: Coincident(g10,g11)
    c: Coincident(g11,g8)
    c: Horizontal(g10)
    c: Vertical(g9)
    c: Symmetric(g8,g8,g-2)
    c: DistanceX(g8,g8) = 20
    c: Equal(g8,g11)
    c: Symmetric(g8,g10,g-1)
    c: Symmetric(g4,g7,g-1)
    c: Symmetric(g7,g6,g-2)
    c: Coincident(g5,g8)
FEATURE [PartDesign::Pad] Pad091
  Direction = (1,1,1)
  Length = 20
  Length2 = 100
  Profile = -> Sketch156
  Refine = true
  Type = 0
FEATURE [Sketcher::SketchObject] Sketch157
  FullyConstrained = true
  MapMode = 5
  Support = -> [XY_Plane132]
  sketch-geometry (4):
    g0: LineSegment StartX=-10.15 StartY=10.15 StartZ=0 EndX=10.15 EndY=10.15 EndZ=0
    g1: LineSegment StartX=10.15 StartY=10.15 StartZ=0 EndX=10.15 EndY=-10.15 EndZ=0
    g2: LineSegment StartX=10.15 StartY=-10.15 StartZ=0 EndX=-10.15 EndY=-10.15 EndZ=0
    g3: LineSegment StartX=-10.15 StartY=-10.15 StartZ=0 EndX=-10.15 EndY=10.15 EndZ=0
  constraints (10):
    c: Coincident(g0,g1)
    c: Coincident(g1,g2)
    c: Coincident(g2,g3)
    c: Coincident(g3,g0)
    c: Horizontal(g2)
    c: Vertical(g3)
    c: Symmetric(g0,g0,g-2)
    c: Symmetric(g0,g1,g-1)
    c: Equal(g1,g0)
    c: DistanceX(g0,g0) = 20.3
FEATURE [PartDesign::Pocket] Pocket056
  BaseFeature = -> Pad091
  Length = 17
  Length2 = 100
  Profile = -> Sketch157
  Refine = true
  Reversed = true
  Type = 0
FEATURE [Sketcher::SketchObject] Sketch158
  FullyConstrained = true
  MapMode = 5
  Placement = pos=(0,0,0) rot=(1,0,0;1.5708rad)
  Support = -> [XZ_Plane131]
  sketch-geometry (1):
    g0: Circle CenterX=0 CenterY=5 CenterZ=0 NormalX=0 NormalY=0 NormalZ=1 AngleXU=0 Radius=2.75
  constraints (3):
    c: PointOnObject(g0,g-2)
    c: DistanceY(g-1,g0) = 5
    c: Diameter(g0) = 5.5
FEATURE [PartDesign::Pocket] Pocket057
  BaseFeature = -> Pocket056
  Length = 5
  Length2 = 100
  Profile = -> Sketch158
  Refine = true
  Type = 1
FEATURE [PartDesign::Fillet] Fillet
  Base = -> Pocket057 [Edge20]
  BaseFeature = -> Pocket057
  Radius = 2
  Refine = true
  SupportTransform = false
FEATURE [PartDesign::Body] Body_25
  Group = -> [LCS_0122,Sketch156,Pad091,Sketch157,Pocket056,Sketch158,Pocket057,Fillet]
  Origin = -> Origin132
  Tip = -> Fillet
COMPONENT P18 — recipe-attached ("HOME_BRACK_Z_1V0", modeled in this document).
Construction recipe (the document's own serialized feature program — sketch geometry with constraints, then the solid features built on it; lengths are millimeters unless a unit is written):

FEATURE [PartDesign::CoordinateSystem] LCS_0112
  AttacherType = Attacher::AttachEngine3D
  MapMode = 2
  Support = -> [X_Axis122]
FEATURE [Sketcher::SketchObject] Sketch144
  FullyConstrained = true
  MapMode = 5
  Support = -> [XY_Plane122]
  sketch-geometry (12):
    g0: Circle CenterX=0 CenterY=0 CenterZ=0 NormalX=0 NormalY=0 NormalZ=1 AngleXU=0 Radius=1.75
    g1: Circle CenterX=0 CenterY=-25 CenterZ=0 NormalX=0 NormalY=0 NormalZ=1 AngleXU=0 Radius=1.75
    g2: Circle CenterX=25 CenterY=-12.5 CenterZ=0 NormalX=0 NormalY=0 NormalZ=1 AngleXU=0 Radius=2.6
    g3: LineSegment StartX=6 StartY=0 StartZ=0 EndX=6 EndY=-31 EndZ=0
    g4: LineSegment StartX=23.5 StartY=-7.5 StartZ=0 EndX=26.5 EndY=-7.5 EndZ=0
    g5: LineSegment StartX=26.5 StartY=-7.5 StartZ=0 EndX=26.5 EndY=3.5 EndZ=0
    g6: LineSegment StartX=26.5 StartY=3.5 StartZ=0 EndX=23.5 EndY=3.5 EndZ=0
    g7: LineSegment StartX=23.5 StartY=3.5 StartZ=0 EndX=23.5 EndY=-7.5 EndZ=0
    g8: LineSegment StartX=-6 StartY=6 StartZ=0 EndX=35 EndY=6 EndZ=0
    g9: LineSegment StartX=35 StartY=6 StartZ=0 EndX=35 EndY=-31 EndZ=0
    g10: LineSegment StartX=35 StartY=-31 StartZ=0 EndX=-6 EndY=-31 EndZ=0
    g11: LineSegment StartX=-6 StartY=-31 StartZ=0 EndX=-6 EndY=6 EndZ=0
  constraints (36):
    c: Coincident(g0,g-1)
    c: PointOnObject(g1,g-2)
    c: DistanceY(g1,g0) = 25
    c: Diameter(g1) = 3.5
    c: Equal(g1,g0)
    c: PointOnObject(g3,g-1)
    c: Vertical(g3)
    c: DistanceX(g-1,g3) = 6
    c: Diameter(g2) = 5.2
    c: DistanceX(g3,g2) = 19
    c: DistanceY(g2,g-1) = 12.5
    c: Coincident(g4,g5)
    c: Coincident(g5,g6)
    c: Coincident(g6,g7)
    c: Coincident(g7,g4)
    c: Horizontal(g4)
    c: Horizontal(g6)
    c: Vertical(g5)
    c: Vertical(g7)
    c: DistanceY(g5,g5) = 11
    c: DistanceY(g2,g4) = 5
    c: DistanceX(g6,g6) = 3
    c: DistanceX(g3,g6) = 17.5
    c: Coincident(g8,g9)
    c: Coincident(g9,g10)
    c: Coincident(g10,g11)
    c: Coincident(g11,g8)
    c: Horizontal(g8)
    c: Horizontal(g10)
    c: Vertical(g9)
    c: Vertical(g11)
    c: DistanceX(g10,g-1) = 6
    c: PointOnObject(g3,g10)
    c: DistanceX(g3,g9) = 29
    c: DistanceY(g10,g1) = 6
    c: DistanceY(g0,g8) = 6
FEATURE [PartDesign::Pad] Pad085
  Direction = (1,1,1)
  Length = 5
  Length2 = 100
  Profile = -> Sketch144
  Refine = true
  Type = 0
FEATURE [PartDesign::Body] Body_23
  Group = -> [LCS_0112,Sketch144,Pad085]
  Origin = -> Origin122
  Tip = -> Pad085
COMPONENT P19 — recipe-attached ("LC_BRACK_B_1V0", modeled in this document).
Construction recipe (the document's own serialized feature program — sketch geometry with constraints, then the solid features built on it; lengths are millimeters unless a unit is written):

FEATURE [PartDesign::CoordinateSystem] LCS_0080
  AttacherType = Attacher::AttachEngine3D
  MapMode = 2
  Support = -> [X_Axis088]
FEATURE [Sketcher::SketchObject] Sketch106
  FullyConstrained = true
  MapMode = 5
  Support = -> [XY_Plane088]
  sketch-geometry (8):
    g0: LineSegment StartX=-38 StartY=0 StartZ=0 EndX=-38 EndY=-11 EndZ=0
    g1: LineSegment StartX=-38 StartY=-11 StartZ=0 EndX=-10 EndY=-11 EndZ=0
    g2: LineSegment StartX=-10 StartY=-11 StartZ=0 EndX=-10 EndY=-45 EndZ=0
    g3: LineSegment StartX=-10 StartY=-45 StartZ=0 EndX=10 EndY=-45 EndZ=0
    g4: LineSegment StartX=10 StartY=-45 StartZ=0 EndX=10 EndY=-11 EndZ=0
    g5: LineSegment StartX=10 StartY=-11 StartZ=0 EndX=30 EndY=-11 EndZ=0
    g6: LineSegment StartX=30 StartY=-11 StartZ=0 EndX=30 EndY=0 EndZ=0
    g7: LineSegment StartX=-38 StartY=0 StartZ=0 EndX=30 EndY=0 EndZ=0
  constraints (23):
    c: PointOnObject(g0,g-1)
    c: Vertical(g0)
    c: Coincident(g0,g1)
    c: Horizontal(g1)
    c: Coincident(g1,g2)
    c: Vertical(g2)
    c: Coincident(g2,g3)
    c: Horizontal(g3)
    c: DistanceX(g3,g3) = 20
    c: DistanceY(g0,g0) = 11
    c: DistanceY(g2,g2) = 34
    c: Coincident(g3,g4)
    c: Vertical(g4)
    c: Coincident(g4,g5)
    c: Horizontal(g5)
    c: Coincident(g5,g6)
    c: Vertical(g6)
    c: Coincident(g7,g0)
    c: Coincident(g7,g6)
    c: DistanceX(g7,g7) = 68
    c: Symmetric(g1,g4,g-2)
    c: DistanceX(g5,g5) = 20
    c: Horizontal(g7)
FEATURE [PartDesign::Pad] Pad067
  Direction = (1,1,1)
  Length = 20
  Length2 = 100
  Midplane = true
  Profile = -> Sketch106
  Refine = true
  Type = 0
FEATURE [Sketcher::SketchObject] Sketch124
  FullyConstrained = true
  MapMode = 5
  Placement = pos=(0,0,0) rot=(1,0,0;1.5708rad)
  Support = -> [XZ_Plane087]
  sketch-geometry (4):
    g0: Circle CenterX=-28 CenterY=0 CenterZ=0 NormalX=0 NormalY=0 NormalZ=1 AngleXU=0 Radius=2.75
    g1: Circle CenterX=20 CenterY=0 CenterZ=0 NormalX=0 NormalY=0 NormalZ=1 AngleXU=0 Radius=2.75
    g2: Circle CenterX=-5 CenterY=0 CenterZ=0 NormalX=0 NormalY=0 NormalZ=1 AngleXU=0 Radius=2.25
    g3: Circle CenterX=5 CenterY=0 CenterZ=0 NormalX=0 NormalY=0 NormalZ=1 AngleXU=0 Radius=2.25
  constraints (11):
    c: PointOnObject(g0,g-1)
    c: PointOnObject(g1,g-1)
    c: PointOnObject(g2,g-1)
    c: Diameter(g3) = 4.5
    c: Equal(g3,g2)
    c: Symmetric(g2,g3,g-2)
    c: DistanceX(g2,g3) = 10
    c: DistanceX(g-1,g1) = 20
    c: DistanceX(g0,g1) = 48
    c: Diameter(g0) = 5.5
    c: Equal(g0,g1)
FEATURE [PartDesign::Pocket] Pocket040
  BaseFeature = -> Pad067
  Length = 5
  Length2 = 100
  Profile = -> Sketch124
  Refine = true
  Reversed = true
  Type = 1
FEATURE [PartDesign::Body] Body_15
  Group = -> [LCS_0080,Sketch106,Pad067,Sketch124,Pocket040]
  Origin = -> Origin088
  Tip = -> Pocket040
COMPONENT P20 — recipe-attached ("LC_BRACK_1V0", modeled in this document).
Construction recipe (the document's own serialized feature program — sketch geometry with constraints, then the solid features built on it; lengths are millimeters unless a unit is written):

FEATURE [Sketcher::SketchObject] Sketch074
  FullyConstrained = true
  MapMode = 5
  Support = -> [XY_Plane061]
  sketch-geometry (10):
    g0: LineSegment StartX=-35 StartY=23 StartZ=0 EndX=-35 EndY=-9 EndZ=0
    g1: LineSegment StartX=-35 StartY=-9 StartZ=0 EndX=35 EndY=-9 EndZ=0
    g2: LineSegment StartX=35 StartY=-9 StartZ=0 EndX=35 EndY=9 EndZ=0
    g3: LineSegment StartX=35 StartY=9 StartZ=0 EndX=-14.5 EndY=9 EndZ=0
    g4: LineSegment StartX=-14.5 StartY=9 StartZ=0 EndX=-14.5 EndY=23 EndZ=0
    g5: LineSegment StartX=-14.5 StartY=23 StartZ=0 EndX=-35 EndY=23 EndZ=0
    g6: Circle CenterX=-29.5 CenterY=16.5 CenterZ=0 NormalX=0 NormalY=0 NormalZ=1 AngleXU=0 Radius=2.25
    g7: Circle CenterX=-19.5 CenterY=16.5 CenterZ=0 NormalX=0 NormalY=0 NormalZ=1 AngleXU=0 Radius=2.25
    g8: Circle CenterX=-25 CenterY=0 CenterZ=0 NormalX=0 NormalY=0 NormalZ=1 AngleXU=0 Radius=3.4
    g9: Circle CenterX=25 CenterY=0 CenterZ=0 NormalX=0 NormalY=0 NormalZ=1 AngleXU=0 Radius=3.4
  constraints (27):
    c: Vertical(g0)
    c: Coincident(g0,g1)
    c: Coincident(g1,g2)
    c: Coincident(g2,g3)
    c: Horizontal(g3)
    c: Coincident(g3,g4)
    c: Vertical(g4)
    c: Coincident(g4,g5)
    c: Coincident(g5,g0)
    c: Horizontal(g5)
    c: Symmetric(g2,g1,g-1)
    c: DistanceY(g2,g2) = 18
    c: DistanceY(g4,g4) = 14
    c: Horizontal(g6,g7)
    c: DistanceX(g6,g7) = 10
    c: DistanceX(g0,g6) = 5.5
    c: DistanceX(g1,g1) = 70
    c: Symmetric(g0,g1,g-2)
    c: DistanceX(g7,g4) = 5
    c: DistanceY(g7,g4) = 6.5
    c: Diameter(g6) = 4.5
    c: Equal(g6,g7)
    c: PointOnObject(g8,g-1)
    c: Diameter(g8) = 6.8
    c: Equal(g8,g9)
    c: DistanceX(g8,g9) = 50
    c: Symmetric(g8,g9,g-2)
FEATURE [PartDesign::Pad] Pad049
  Direction = (1,1,1)
  Length = 10
  Length2 = 100
  Profile = -> Sketch074
  Type = 0
FEATURE [PartDesign::CoordinateSystem] LCS_0055
  AttacherType = Attacher::AttachEngine3D
  MapMode = 2
  Support = -> [X_Axis061]
FEATURE [Sketcher::SketchObject] Sketch075
  FullyConstrained = true
  MapMode = 5
  Support = -> [XY_Plane061]
  sketch-geometry (2):
    g0: Circle CenterX=-25 CenterY=0 CenterZ=0 NormalX=0 NormalY=0 NormalZ=1 AngleXU=0 Radius=6.5
    g1: Circle CenterX=25 CenterY=0 CenterZ=0 NormalX=0 NormalY=0 NormalZ=1 AngleXU=0 Radius=6.5
  constraints (5):
    c: PointOnObject(g0,g-1)
    c: Diameter(g0) = 13
    c: Equal(g0,g1)
    c: Symmetric(g0,g1,g-2)
    c: DistanceX(g0,g1) = 50
FEATURE [PartDesign::Pocket] Pocket021
  BaseFeature = -> Pad049
  Length = 2
  Length2 = 100
  Profile = -> Sketch075
  Reversed = true
  Type = 0
FEATURE [PartDesign::Body] Body_019
  Group = -> [LCS_0055,Sketch074,Pad049,Sketch075,Pocket021]
  Origin = -> Origin061
  Tip = -> Pocket021
COMPONENT P21 — recipe-attached ("LC_BRACK_A_1V0", modeled in this document).
Construction recipe (the document's own serialized feature program — sketch geometry with constraints, then the solid features built on it; lengths are millimeters unless a unit is written):

FEATURE [PartDesign::CoordinateSystem] LCS_0052
  AttacherType = Attacher::AttachEngine3D
  MapMode = 2
  Support = -> [X_Axis058]
FEATURE [Sketcher::SketchObject] Sketch069
  FullyConstrained = true
  MapMode = 5
  Support = -> [XY_Plane058]
  sketch-geometry (10):
    g0: LineSegment StartX=-35 StartY=23 StartZ=0 EndX=-35 EndY=-9 EndZ=0
    g1: LineSegment StartX=-35 StartY=-9 StartZ=0 EndX=35 EndY=-9 EndZ=0
    g2: LineSegment StartX=35 StartY=-9 StartZ=0 EndX=35 EndY=9 EndZ=0
    g3: LineSegment StartX=35 StartY=9 StartZ=0 EndX=-14.5 EndY=9 EndZ=0
    g4: LineSegment StartX=-14.5 StartY=9 StartZ=0 EndX=-14.5 EndY=23 EndZ=0
    g5: LineSegment StartX=-14.5 StartY=23 StartZ=0 EndX=-35 EndY=23 EndZ=0
    g6: Circle CenterX=-29.5 CenterY=16.5 CenterZ=0 NormalX=0 NormalY=0 NormalZ=1 AngleXU=0 Radius=2.25
    g7: Circle CenterX=-19.5 CenterY=16.5 CenterZ=0 NormalX=0 NormalY=0 NormalZ=1 AngleXU=0 Radius=2.25
    g8: Circle CenterX=-25 CenterY=0 CenterZ=0 NormalX=0 NormalY=0 NormalZ=1 AngleXU=0 Radius=3.4
    g9: Circle CenterX=25 CenterY=0 CenterZ=0 NormalX=0 NormalY=0 NormalZ=1 AngleXU=0 Radius=3.4
  constraints (27):
    c: Vertical(g0)
    c: Coincident(g0,g1)
    c: Coincident(g1,g2)
    c: Coincident(g2,g3)
    c: Horizontal(g3)
    c: Coincident(g3,g4)
    c: Vertical(g4)
    c: Coincident(g4,g5)
    c: Coincident(g5,g0)
    c: Horizontal(g5)
    c: Symmetric(g2,g1,g-1)
    c: DistanceY(g2,g2) = 18
    c: DistanceY(g4,g4) = 14
    c: Horizontal(g6,g7)
    c: DistanceX(g6,g7) = 10
    c: DistanceX(g0,g6) = 5.5
    c: DistanceX(g1,g1) = 70
    c: Symmetric(g0,g1,g-2)
    c: DistanceX(g7,g4) = 5
    c: DistanceY(g7,g4) = 6.5
    c: Diameter(g6) = 4.5
    c: Equal(g6,g7)
    c: PointOnObject(g8,g-1)
    c: Diameter(g8) = 6.8
    c: Equal(g8,g9)
    c: DistanceX(g8,g9) = 50
    c: Symmetric(g8,g9,g-2)
FEATURE [PartDesign::Pad] Pad046
  Direction = (1,1,1)
  Length = 10
  Length2 = 100
  Profile = -> Sketch069
  Type = 0
FEATURE [Sketcher::SketchObject] Sketch070
  FullyConstrained = true
  MapMode = 5
  Support = -> [XY_Plane058]
  sketch-geometry (2):
    g0: Circle CenterX=-25 CenterY=0 CenterZ=0 NormalX=0 NormalY=0 NormalZ=1 AngleXU=0 Radius=6.5
    g1: Circle CenterX=25 CenterY=0 CenterZ=0 NormalX=0 NormalY=0 NormalZ=1 AngleXU=0 Radius=6.5
  constraints (5):
    c: PointOnObject(g0,g-1)
    c: Diameter(g0) = 13
    c: Equal(g0,g1)
    c: Symmetric(g0,g1,g-2)
    c: DistanceX(g0,g1) = 50
FEATURE [PartDesign::Pocket] Pocket019
  BaseFeature = -> Pad046
  Length = 2
  Length2 = 100
  Profile = -> Sketch070
  Reversed = true
  Type = 0
FEATURE [PartDesign::Body] Body_7
  Group = -> [LCS_0052,Sketch069,Pad046,Sketch070,Pocket019]
  Origin = -> Origin058
  Tip = -> Pocket019
COMPONENT P22 — recipe-attached ("LC_PCB_BRACK_1V0", modeled in this document).
Construction recipe (the document's own serialized feature program — sketch geometry with constraints, then the solid features built on it; lengths are millimeters unless a unit is written):

FEATURE [PartDesign::CoordinateSystem] LCS_0082
  AttacherType = Attacher::AttachEngine3D
  MapMode = 2
  Support = -> [X_Axis090]
FEATURE [Sketcher::SketchObject] Sketch112
  FullyConstrained = true
  MapMode = 5
  Support = -> [XY_Plane090]
  sketch-geometry (6):
    g0: LineSegment StartX=-12 StartY=-10 StartZ=0 EndX=12 EndY=-10 EndZ=0
    g1: LineSegment StartX=12 StartY=-10 StartZ=0 EndX=12 EndY=58 EndZ=0
    g2: LineSegment StartX=12 StartY=58 StartZ=0 EndX=-12 EndY=58 EndZ=0
    g3: LineSegment StartX=-12 StartY=58 StartZ=0 EndX=-12 EndY=-10 EndZ=0
    g4: Circle CenterX=0 CenterY=0 CenterZ=0 NormalX=0 NormalY=0 NormalZ=1 AngleXU=0 Radius=2.75
    g5: Circle CenterX=0 CenterY=48 CenterZ=0 NormalX=0 NormalY=0 NormalZ=1 AngleXU=0 Radius=2.75
  constraints (16):
    c: Coincident(g0,g1)
    c: Coincident(g1,g2)
    c: Coincident(g2,g3)
    c: Coincident(g3,g0)
    c: Horizontal(g2)
    c: Vertical(g1)
    c: Vertical(g3)
    c: Coincident(g4,g-1)
    c: Diameter(g4) = 5.5
    c: Symmetric(g0,g0,g-2)
    c: DistanceX(g0,g0) = 24
    c: DistanceY(g0,g-1) = 10
    c: DistanceY(g1,g1) = 68
    c: PointOnObject(g5,g-2)
    c: Equal(g5,g4)
    c: DistanceY(g5,g1) = 10
FEATURE [PartDesign::Pad] Pad069
  Direction = (1,1,1)
  Length = 5
  Length2 = 100
  Profile = -> Sketch112
  Refine = true
  Type = 0
FEATURE [Sketcher::SketchObject] Sketch159
  AttachmentOffset = pos=(0,0,5) rot=(0,0,1;0rad)
  FullyConstrained = true
  MapMode = 5
  Placement = pos=(0,0,5) rot=(0,0,1;0rad)
  Support = -> [XY_Plane090]
  sketch-geometry (12):
    g0: LineSegment StartX=-10 StartY=7 StartZ=0 EndX=10 EndY=7 EndZ=0
    g1: LineSegment StartX=10 StartY=7 StartZ=0 EndX=10 EndY=41 EndZ=0
    g2: LineSegment StartX=10 StartY=41 StartZ=0 EndX=-10 EndY=41 EndZ=0
    g3: LineSegment StartX=-10 StartY=41 StartZ=0 EndX=-10 EndY=7 EndZ=0
    g4: LineSegment StartX=-10 StartY=39 StartZ=0 EndX=10 EndY=39 EndZ=0
    g5: LineSegment StartX=10 StartY=39 StartZ=0 EndX=10 EndY=35 EndZ=0
    g6: LineSegment StartX=10 StartY=35 StartZ=0 EndX=-10 EndY=35 EndZ=0
    g7: LineSegment StartX=-10 StartY=35 StartZ=0 EndX=-10 EndY=39 EndZ=0
    g8: LineSegment StartX=-10 StartY=13 StartZ=0 EndX=10 EndY=13 EndZ=0
    g9: LineSegment StartX=10 StartY=13 StartZ=0 EndX=10 EndY=9 EndZ=0
    g10: LineSegment StartX=10 StartY=9 StartZ=0 EndX=-10 EndY=9 EndZ=0
    g11: LineSegment StartX=-10 StartY=9 StartZ=0 EndX=-10 EndY=13 EndZ=0
  constraints (35):
    c: Coincident(g0,g1)
    c: Coincident(g1,g2)
    c: Coincident(g2,g3)
    c: Coincident(g3,g0)
    c: Horizontal(g0)
    c: Vertical(g1)
    c: Vertical(g3)
    c: Symmetric(g1,g2,g-2)
    c: DistanceY(g-1,g0) = 7
    c: DistanceY(g1,g1) = 34
    c: DistanceX(g2,g2) = 20
    c: Coincident(g4,g5)
    c: Coincident(g5,g6)
    c: Coincident(g6,g7)
    c: Coincident(g7,g4)
    c: Horizontal(g4)
    c: Horizontal(g6)
    c: Vertical(g5)
    c: Vertical(g7)
    c: PointOnObject(g4,g3)
    c: PointOnObject(g5,g1)
    c: Coincident(g8,g9)
    c: Coincident(g9,g10)
    c: Coincident(g10,g11)
    c: Coincident(g11,g8)
    c: Horizontal(g8)
    c: Horizontal(g10)
    c: Vertical(g9)
    c: Vertical(g11)
    c: PointOnObject(g8,g3)
    c: PointOnObject(g9,g1)
    c: DistanceY(g0,g9) = 2
    c: DistanceY(g9,g9) = 4
    c: DistanceY(g4,g1) = 2
    c: DistanceY(g5,g5) = 4
FEATURE [PartDesign::Pocket] Pocket058
  BaseFeature = -> Pad069
  Length = 2
  Length2 = 100
  Profile = -> Sketch159
  Refine = true
  Type = 0
FEATURE [PartDesign::Body] Body_8
  Group = -> [LCS_0082,Sketch112,Pad069,Sketch159,Pocket058]
  Origin = -> Origin090
  Tip = -> Pocket058
COMPONENT P23 — recipe-attached ("LEAD_SCREW_Z_1V0", modeled in this document).
Construction recipe (the document's own serialized feature program — sketch geometry with constraints, then the solid features built on it; lengths are millimeters unless a unit is written):

FEATURE [PartDesign::CoordinateSystem] LCS_0041
  AttacherType = Attacher::AttachEngine3D
  MapMode = 2
  Support = -> [X_Axis046]
FEATURE [Sketcher::SketchObject] Sketch051
  FullyConstrained = true
  MapMode = 5
  Support = -> [XY_Plane046]
  sketch-geometry (1):
    g0: Circle CenterX=0 CenterY=0 CenterZ=0 NormalX=0 NormalY=0 NormalZ=1 AngleXU=0 Radius=4
  constraints (2):
    c: Coincident(g0,g-1)
    c: Diameter(g0) = 8
FEATURE [PartDesign::Pad] Pad037
  Direction = (1,1,1)
  Length = 450
  Length2 = 100
  Profile = -> Sketch051
  Refine = true
  Type = 0
FEATURE [PartDesign::Body] Body_5
  Group = -> [LCS_0041,Sketch051,Pad037]
  Origin = -> Origin046
  Tip = -> Pad037
COMPONENT P24 — recipe-attached ("LEAD_SCREW_X_1V0", modeled in this document).
Construction recipe (the document's own serialized feature program — sketch geometry with constraints, then the solid features built on it; lengths are millimeters unless a unit is written):

FEATURE [Sketcher::SketchObject] Sketch092
  FullyConstrained = true
  MapMode = 5
  Support = -> [XY_Plane075]
  sketch-geometry (1):
    g0: Circle CenterX=0 CenterY=0 CenterZ=0 NormalX=0 NormalY=0 NormalZ=1 AngleXU=0 Radius=4
  constraints (2):
    c: Coincident(g0,g-1)
    c: Diameter(g0) = 8
FEATURE [PartDesign::CoordinateSystem] LCS_0069
  AttacherType = Attacher::AttachEngine3D
  MapMode = 2
  Support = -> [X_Axis076]
FEATURE [PartDesign::Pad] Pad059
  Direction = (1,1,1)
  Length = 450
  Length2 = 100
  Profile = -> Sketch092
  Refine = true
  Type = 0
FEATURE [PartDesign::Body] Body_024
  Group = -> [LCS_0069,Sketch092,Pad059]
  Origin = -> Origin076
  Tip = -> Pad059
COMPONENT P25 — recipe-attached ("MAGNET_COUPLER_1V0", modeled in this document).
Construction recipe (the document's own serialized feature program — sketch geometry with constraints, then the solid features built on it; lengths are millimeters unless a unit is written):

FEATURE [PartDesign::CoordinateSystem] LCS_0106
  AttacherType = Attacher::AttachEngine3D
  MapMode = 2
  Support = -> [X_Axis114]
FEATURE [Sketcher::SketchObject] Sketch136
  FullyConstrained = true
  MapMode = 5
  Support = -> [XY_Plane114]
  sketch-geometry (1):
    g0: Circle CenterX=0 CenterY=0 CenterZ=0 NormalX=0 NormalY=0 NormalZ=1 AngleXU=0 Radius=9
  constraints (2):
    c: Coincident(g0,g-1)
    c: Diameter(g0) = 18
FEATURE [PartDesign::Pad] Pad081
  Direction = (1,1,1)
  Length = 13
  Length2 = 100
  Profile = -> Sketch136
  Refine = true
  Type = 0
FEATURE [Sketcher::SketchObject] Sketch137
  FullyConstrained = true
  MapMode = 5
  Support = -> [XY_Plane114]
  sketch-geometry (6):
    g0: Circle CenterX=0 CenterY=0 CenterZ=0 NormalX=0 NormalY=0 NormalZ=1 AngleXU=0 Radius=4.25
    g1: LineSegment StartX=-3.15278 StartY=2.85 StartZ=0 EndX=-6.25 EndY=2.85 EndZ=0
    g2: LineSegment StartX=-6.25 StartY=2.85 StartZ=0 EndX=-6.25 EndY=-2.85 EndZ=0
    g3: LineSegment StartX=-6.25 StartY=-2.85 StartZ=0 EndX=-3.15278 EndY=-2.85 EndZ=0
    g4: GeomPoint X=-4.25 Y=0 Z=0
    g5: ArcOfCircle CenterX=0 CenterY=-7e-16 CenterZ=0 NormalX=0 NormalY=0 NormalZ=1 AngleXU=0 Radius=4.25 StartAngle=3.87659 EndAngle=8.68978
  constraints (15):
    c: Coincident(g0,g-1)
    c: Diameter(g0) = 8.5
    c: PointOnObject(g1,g0)
    c: Horizontal(g1)
    c: Coincident(g1,g2)
    c: Coincident(g2,g3)
    c: PointOnObject(g3,g0)
    c: Horizontal(g3)
    c: PointOnObject(g4,g0)
    c: PointOnObject(g4,g-1)
    c: DistanceX(g1,g4) = 2
    c: Symmetric(g1,g2,g-1)
    c: Coincident(g5,g-1)
    c: Coincident(g5,g1)
    c: Coincident(g5,g3)
FEATURE [PartDesign::Pocket] Pocket045
  BaseFeature = -> Pad081
  Length = 8
  Length2 = 100
  Profile = -> Sketch137
  Refine = true
  Reversed = true
  Type = 0
FEATURE [Sketcher::SketchObject] Sketch138
  AttachmentOffset = pos=(0,0,13) rot=(0,0,1;0rad)
  FullyConstrained = true
  MapMode = 5
  Placement = pos=(0,0,13) rot=(0,0,1;0rad)
  Support = -> [XY_Plane114]
  sketch-geometry (1):
    g0: Circle CenterX=0 CenterY=0 CenterZ=0 NormalX=0 NormalY=0 NormalZ=1 AngleXU=0 Radius=3.1
  constraints (2):
    c: Coincident(g0,g-1)
    c: Diameter(g0) = 6.2
FEATURE [PartDesign::Pocket] Pocket046
  BaseFeature = -> Pocket045
  Length = 2.6
  Length2 = 100
  Profile = -> Sketch138
  Refine = true
  Type = 0
FEATURE [Sketcher::SketchObject] Sketch139
  FullyConstrained = true
  MapMode = 5
  Placement = pos=(0,0,0) rot=(0.57735,0.57735,0.57735;2.0944rad)
  Support = -> [YZ_Plane114]
  sketch-geometry (1):
    g0: Circle CenterX=0 CenterY=4 CenterZ=0 NormalX=0 NormalY=0 NormalZ=1 AngleXU=0 Radius=1.75
  constraints (3):
    c: PointOnObject(g0,g-2)
    c: Diameter(g0) = 3.5
    c: DistanceY(g-1,g0) = 4
FEATURE [PartDesign::Pocket] Pocket047
  BaseFeature = -> Pocket046
  Length = 5
  Length2 = 100
  Profile = -> Sketch139
  Refine = true
  Type = 1
FEATURE [PartDesign::Body] Body_20
  Group = -> [LCS_0106,Sketch136,Pad081,Sketch137,Pocket045,Sketch138,Pocket046,Sketch139,Pocket047]
  Origin = -> Origin114
  Tip = -> Pocket047
COMPONENT P26 — recipe-attached ("MAG_SW_1V0", modeled in this document).
Construction recipe (the document's own serialized feature program — sketch geometry with constraints, then the solid features built on it; lengths are millimeters unless a unit is written):

FEATURE [PartDesign::CoordinateSystem] LCS_0110
  AttacherType = Attacher::AttachEngine3D
  MapMode = 2
  Support = -> [X_Axis120]
FEATURE [Sketcher::SketchObject] Sketch142
  FullyConstrained = true
  MapMode = 5
  Support = -> [XY_Plane120]
  sketch-geometry (5):
    g0: Circle CenterX=0 CenterY=0 CenterZ=0 NormalX=0 NormalY=0 NormalZ=1 AngleXU=0 Radius=2.6
    g1: LineSegment StartX=-10 StartY=9.5 StartZ=0 EndX=10 EndY=9.5 EndZ=0
    g2: LineSegment StartX=10 StartY=9.5 StartZ=0 EndX=10 EndY=-15.5 EndZ=0
    g3: LineSegment StartX=10 StartY=-15.5 StartZ=0 EndX=-10 EndY=-15.5 EndZ=0
    g4: LineSegment StartX=-10 StartY=-15.5 StartZ=0 EndX=-10 EndY=9.5 EndZ=0
  constraints (13):
    c: Coincident(g0,g-1)
    c: Coincident(g1,g2)
    c: Coincident(g2,g3)
    c: Coincident(g3,g4)
    c: Coincident(g4,g1)
    c: Horizontal(g3)
    c: Vertical(g2)
    c: Vertical(g4)
    c: Symmetric(g1,g1,g-2)
    c: DistanceX(g1,g1) = 20
    c: Diameter(g0) = 5.2
    c: DistanceY(g2,g2) = 25
    c: DistanceY(g-1,g1) = 9.5
FEATURE [PartDesign::Pad] Pad084
  Direction = (1,1,1)
  Length = 1.6
  Length2 = 100
  Profile = -> Sketch142
  Refine = true
  Type = 0
FEATURE [PartDesign::Body] Body_22
  Group = -> [LCS_0110,Sketch142,Pad084]
  Origin = -> Origin120
  Tip = -> Pad084
COMPONENT P27 — recipe-attached ("MTR_BRACK_X_1V0", modeled in this document).
Construction recipe (the document's own serialized feature program — sketch geometry with constraints, then the solid features built on it; lengths are millimeters unless a unit is written):

FEATURE [PartDesign::CoordinateSystem] LCS_0039
  AttacherType = Attacher::AttachEngine3D
  MapMode = 2
  Support = -> [X_Axis044]
FEATURE [Sketcher::SketchObject] Sketch048
  FullyConstrained = true
  MapMode = 5
  Support = -> [XY_Plane044]
  sketch-geometry (22):
    g0: Circle CenterX=0 CenterY=0 CenterZ=0 NormalX=0 NormalY=0 NormalZ=1 AngleXU=0 Radius=11.25
    g1: Circle CenterX=0 CenterY=0 CenterZ=0 NormalX=0 NormalY=0 NormalZ=1 AngleXU=0 Radius=21.9203
    g2: LineSegment StartX=-15.5 StartY=15.5 StartZ=0 EndX=15.5 EndY=15.5 EndZ=0
    g3: LineSegment StartX=15.5 StartY=15.5 StartZ=0 EndX=15.5 EndY=-15.5 EndZ=0
    g4: LineSegment StartX=15.5 StartY=-15.5 StartZ=0 EndX=-15.5 EndY=-15.5 EndZ=0
    g5: LineSegment StartX=-15.5 StartY=-15.5 StartZ=0 EndX=-15.5 EndY=15.5 EndZ=0
    g6: Circle CenterX=-15.5 CenterY=15.5 CenterZ=0 NormalX=0 NormalY=0 NormalZ=1 AngleXU=0 Radius=1.75
    g7: Circle CenterX=15.5 CenterY=15.5 CenterZ=0 NormalX=0 NormalY=0 NormalZ=1 AngleXU=0 Radius=1.75
    g8: Circle CenterX=15.5 CenterY=-15.5 CenterZ=0 NormalX=0 NormalY=0 NormalZ=1 AngleXU=0 Radius=1.75
    g9: Circle CenterX=-15.5 CenterY=-15.5 CenterZ=0 NormalX=0 NormalY=0 NormalZ=1 AngleXU=0 Radius=1.75
    g10: LineSegment StartX=40 StartY=-31 StartZ=0 EndX=-40 EndY=-31 EndZ=0
    g11: LineSegment StartX=-21.15 StartY=21.15 StartZ=0 EndX=21.15 EndY=21.15 EndZ=0
    g12: LineSegment StartX=21.15 StartY=21.15 StartZ=0 EndX=21.15 EndY=-21.15 EndZ=0
    g13: LineSegment StartX=21.15 StartY=-21.15 StartZ=0 EndX=-21.15 EndY=-21.15 EndZ=0
    g14: LineSegment StartX=-21.15 StartY=-21.15 StartZ=0 EndX=-21.15 EndY=21.15 EndZ=0
    g15: Circle CenterX=-30 CenterY=-21 CenterZ=0 NormalX=0 NormalY=0 NormalZ=1 AngleXU=0 Radius=2.75
    g16: Circle CenterX=30 CenterY=-21 CenterZ=0 NormalX=0 NormalY=0 NormalZ=1 AngleXU=0 Radius=2.75
    g17: LineSegment StartX=-40 StartY=-31 StartZ=0 EndX=-40 EndY=-11 EndZ=0
    g18: LineSegment StartX=-40 StartY=-11 StartZ=0 EndX=-21 EndY=21 EndZ=0
    g19: LineSegment StartX=21 StartY=21 StartZ=0 EndX=40 EndY=-11 EndZ=0
    g20: LineSegment StartX=40 StartY=-11 StartZ=0 EndX=40 EndY=-31 EndZ=0
    g21: LineSegment StartX=-21 StartY=21 StartZ=0 EndX=21 EndY=21 EndZ=0
  constraints (55):
    c: Coincident(g0,g-1)
    c: Diameter(g0) = 22.5
    c: Coincident(g1,g0)
    c: Coincident(g2,g3)
    c: Coincident(g3,g4)
    c: Coincident(g4,g5)
    c: Coincident(g5,g2)
    c: Horizontal(g2)
    c: Horizontal(g4)
    c: Vertical(g3)
    c: Vertical(g5)
    c: PointOnObject(g2,g1)
    c: PointOnObject(g3,g1)
    c: Equal(g3,g2)
    c: PointOnObject(g2,g1)
    c: Coincident(g6,g2)
    c: Coincident(g7,g2)
    c: Coincident(g8,g3)
    c: Coincident(g9,g4)
    c: Diameter(g9) = 3.5
    c: Equal(g9,g8)
    c: Equal(g9,g7)
    c: Equal(g9,g6)
    c: DistanceY(g3,g3) = 31
    c: Coincident(g11,g12)
    c: Coincident(g12,g13)
    c: Coincident(g13,g14)
    c: Coincident(g14,g11)
    c: Horizontal(g11)
    c: Vertical(g14)
    c: Symmetric(g13,g12,g-2)
    c: Symmetric(g12,g11,g-1)
    c: Equal(g12,g13)
    c: DistanceX(g11,g11) = 42.3
    c: DistanceY(g10,g-1) = 31
    c: Symmetric(g19,g18,g-2)
    c: DistanceX(g18,g19) = 42
    c: Diameter(g16) = 5.5
    c: Equal(g16,g15)
    c: Symmetric(g15,g16,g-2)
    c: DistanceX(g15,g16) = 60
    c: DistanceY(g10,g16) = 10
    c: Coincident(g10,g17)
    c: Vertical(g17)
    c: Coincident(g17,g18)
    c: Coincident(g19,g20)
    c: Coincident(g20,g10)
    c: Vertical(g20)
    c: Coincident(g21,g18)
    c: Coincident(g21,g19)
    c: DistanceY(g-1,g19) = 21
    c: DistanceX(g10,g10) = 80
    c: Symmetric(g10,g10,g-2)
    c: DistanceY(g17,g17) = 20
    c: Horizontal(g17,g19)
FEATURE [PartDesign::Pad] Pad036
  Direction = (1,1,1)
  Length = 8
  Length2 = 100
  Profile = -> Sketch048
  Refine = true
  Type = 0
FEATURE [Sketcher::SketchObject] Sketch135
  FullyConstrained = true
  MapMode = 5
  Support = -> [XY_Plane044]
  sketch-geometry (13):
    g0: Circle CenterX=0 CenterY=0 CenterZ=0 NormalX=0 NormalY=0 NormalZ=1 AngleXU=0 Radius=21.9203
    g1: LineSegment StartX=-15.5 StartY=15.5 StartZ=0 EndX=15.5 EndY=15.5 EndZ=0
    g2: LineSegment StartX=15.5 StartY=15.5 StartZ=0 EndX=15.5 EndY=-15.5 EndZ=0
    g3: LineSegment StartX=15.5 StartY=-15.5 StartZ=0 EndX=-15.5 EndY=-15.5 EndZ=0
    g4: LineSegment StartX=-15.5 StartY=-15.5 StartZ=0 EndX=-15.5 EndY=15.5 EndZ=0
    g5: Circle CenterX=-15.5 CenterY=15.5 CenterZ=0 NormalX=0 NormalY=0 NormalZ=1 AngleXU=0 Radius=1.75
    g6: Circle CenterX=15.5 CenterY=15.5 CenterZ=0 NormalX=0 NormalY=0 NormalZ=1 AngleXU=0 Radius=1.75
    g7: Circle CenterX=15.5 CenterY=-15.5 CenterZ=0 NormalX=0 NormalY=0 NormalZ=1 AngleXU=0 Radius=1.75
    g8: Circle CenterX=-15.5 CenterY=-15.5 CenterZ=0 NormalX=0 NormalY=0 NormalZ=1 AngleXU=0 Radius=1.75
    g9: LineSegment StartX=-21.15 StartY=21.15 StartZ=0 EndX=21.15 EndY=21.15 EndZ=0
    g10: LineSegment StartX=21.15 StartY=21.15 StartZ=0 EndX=21.15 EndY=-21.15 EndZ=0
    g11: LineSegment StartX=21.15 StartY=-21.15 StartZ=0 EndX=-21.15 EndY=-21.15 EndZ=0
    g12: LineSegment StartX=-21.15 StartY=-21.15 StartZ=0 EndX=-21.15 EndY=21.15 EndZ=0
  constraints (32):
    c: Coincident(g1,g2)
    c: Coincident(g2,g3)
    c: Coincident(g3,g4)
    c: Coincident(g4,g1)
    c: Horizontal(g1)
    c: Horizontal(g3)
    c: Vertical(g2)
    c: Vertical(g4)
    c: PointOnObject(g1,g0)
    c: PointOnObject(g2,g0)
    c: Equal(g2,g1)
    c: PointOnObject(g1,g0)
    c: Coincident(g5,g1)
    c: Coincident(g6,g1)
    c: Coincident(g7,g2)
    c: Coincident(g8,g3)
    c: Diameter(g8) = 3.5
    c: Equal(g8,g7)
    c: Equal(g8,g6)
    c: Equal(g8,g5)
    c: DistanceY(g2,g2) = 31
    c: Coincident(g9,g10)
    c: Coincident(g10,g11)
    c: Coincident(g11,g12)
    c: Coincident(g12,g9)
    c: Horizontal(g9)
    c: Vertical(g12)
    c: Symmetric(g11,g10,g-2)
    c: Symmetric(g10,g9,g-1)
    c: Equal(g10,g11)
    c: DistanceX(g9,g9) = 42.3
    c: Coincident(g-1,g0)
FEATURE [PartDesign::Hole] Hole003
  BaseFeature = -> Pad036
  Depth = 25
  DepthType = 1
  Diameter = 3.4
  DrillForDepth = false
  DrillPoint = 1
  DrillPointAngle = 118
  HoleCutCountersinkAngle = 90
  HoleCutCustomValues = false
  HoleCutDepth = 0
  HoleCutDiameter = 6.7
  HoleCutType = 7
  ModelActualThread = false
  Profile = -> Sketch135
  Refine = true
  Reversed = true
  Tapered = false
  TaperedAngle = 90
  ThreadAngle = 0
  ThreadClass = 0
  ThreadCutOffInner = 0
  ThreadCutOffOuter = 0
  ThreadDirection = 0
  ThreadFit = 0
  ThreadPitch = 0
  ThreadSize = 9
  ThreadType = 1
  Threaded = false
FEATURE [PartDesign::Body] Body_4
  Group = -> [LCS_0039,Sketch048,Pad036,Sketch135,Hole003]
  Origin = -> Origin044
  Tip = -> Hole003
COMPONENT P28 — recipe-attached ("MTR_BRACK_Z_1V0", modeled in this document).
Construction recipe (the document's own serialized feature program — sketch geometry with constraints, then the solid features built on it; lengths are millimeters unless a unit is written):

FEATURE [PartDesign::CoordinateSystem] LCS_0084
  AttacherType = Attacher::AttachEngine3D
  MapMode = 2
  Support = -> [X_Axis092]
FEATURE [Sketcher::SketchObject] Sketch113
  FullyConstrained = true
  MapMode = 5
  Support = -> [XY_Plane092]
  sketch-geometry (18):
    g0: LineSegment StartX=27 StartY=-13 StartZ=0 EndX=27 EndY=47 EndZ=0
    g1: LineSegment StartX=27 StartY=47 StartZ=0 EndX=-27 EndY=47 EndZ=0
    g2: LineSegment StartX=-27 StartY=47 StartZ=0 EndX=-27 EndY=-13 EndZ=0
    g3: Circle CenterX=0 CenterY=26 CenterZ=0 NormalX=0 NormalY=0 NormalZ=1 AngleXU=0 Radius=11.25
    g4: LineSegment StartX=-21.15 StartY=47.15 StartZ=0 EndX=21.15 EndY=47.15 EndZ=0
    g5: LineSegment StartX=21.15 StartY=47.15 StartZ=0 EndX=21.15 EndY=4.85 EndZ=0
    g6: LineSegment StartX=21.15 StartY=4.85 StartZ=0 EndX=-21.15 EndY=4.85 EndZ=0
    g7: LineSegment StartX=-21.15 StartY=4.85 StartZ=0 EndX=-21.15 EndY=47.15 EndZ=0
    g8: LineSegment StartX=-21.15 StartY=47.15 StartZ=0 EndX=21.15 EndY=4.85 EndZ=0
    g9: LineSegment StartX=-15.5 StartY=41.5 StartZ=0 EndX=15.5 EndY=41.5 EndZ=0
    g10: LineSegment StartX=15.5 StartY=41.5 StartZ=0 EndX=15.5 EndY=10.5 EndZ=0
    g11: LineSegment StartX=15.5 StartY=10.5 StartZ=0 EndX=-15.5 EndY=10.5 EndZ=0
    g12: LineSegment StartX=-15.5 StartY=10.5 StartZ=0 EndX=-15.5 EndY=41.5 EndZ=0
    g13: Circle CenterX=-15.5 CenterY=41.5 CenterZ=0 NormalX=0 NormalY=0 NormalZ=1 AngleXU=0 Radius=1.75
    g14: Circle CenterX=15.5 CenterY=41.5 CenterZ=0 NormalX=0 NormalY=0 NormalZ=1 AngleXU=0 Radius=1.75
    g15: Circle CenterX=15.5 CenterY=10.5 CenterZ=0 NormalX=0 NormalY=0 NormalZ=1 AngleXU=0 Radius=1.75
    g16: Circle CenterX=-15.5 CenterY=10.5 CenterZ=0 NormalX=0 NormalY=0 NormalZ=1 AngleXU=0 Radius=1.75
    g17: LineSegment StartX=-27 StartY=-13 StartZ=0 EndX=27 EndY=-13 EndZ=0
  constraints (46):
    c: Coincident(g0,g1)
    c: Coincident(g1,g2)
    c: Vertical(g0)
    c: Vertical(g2)
    c: Symmetric(g1,g0,g-2)
    c: PointOnObject(g3,g-2)
    c: Diameter(g3) = 22.5
    c: DistanceY(g-1,g3) = 26
    c: Coincident(g4,g5)
    c: Coincident(g5,g6)
    c: Coincident(g6,g7)
    c: Coincident(g7,g4)
    c: Horizontal(g6)
    c: Vertical(g5)
    c: Vertical(g7)
    c: Symmetric(g4,g4,g-2)
    c: DistanceX(g4,g4) = 42.3
    c: Equal(g7,g4)
    c: Coincident(g8,g4)
    c: Coincident(g8,g5)
    c: PointOnObject(g3,g8)
    c: Coincident(g9,g10)
    c: Coincident(g10,g11)
    c: Coincident(g11,g12)
    c: Coincident(g12,g9)
    c: Horizontal(g11)
    c: Vertical(g10)
    c: Vertical(g12)
    c: PointOnObject(g9,g8)
    c: PointOnObject(g10,g8)
    c: DistanceX(g9,g9) = 31
    c: Symmetric(g9,g9,g-2)
    c: Coincident(g13,g9)
    c: Coincident(g14,g9)
    c: Coincident(g15,g10)
    c: Coincident(g16,g11)
    c: Diameter(g16) = 3.5
    c: Equal(g16,g13)
    c: Equal(g16,g14)
    c: Equal(g16,g15)
    c: DistanceX(g2,g0) = 54
    c: DistanceY(g-1,g0) = 47
    c: Coincident(g17,g2)
    c: Coincident(g17,g0)
    c: Horizontal(g17)
    c: DistanceY(g0,g-1) = 13
FEATURE [PartDesign::Pad] Pad070
  Direction = (1,1,1)
  Length = 40
  Length2 = 100
  Profile = -> Sketch113
  Refine = true
  Type = 0
FEATURE [Sketcher::SketchObject] Sketch125
  AttachmentOffset = pos=(0,0,22) rot=(0,0,1;0rad)
  FullyConstrained = true
  MapMode = 5
  Placement = pos=(0,0,22) rot=(0,0,1;0rad)
  Support = -> [XY_Plane092]
  sketch-geometry (4):
    g0: LineSegment StartX=-22 StartY=50 StartZ=0 EndX=22 EndY=50 EndZ=0
    g1: LineSegment StartX=22 StartY=50 StartZ=0 EndX=22 EndY=0 EndZ=0
    g2: LineSegment StartX=22 StartY=0 StartZ=0 EndX=-22 EndY=0 EndZ=0
    g3: LineSegment StartX=-22 StartY=0 StartZ=0 EndX=-22 EndY=50 EndZ=0
  constraints (11):
    c: Coincident(g0,g1)
    c: Coincident(g1,g2)
    c: Coincident(g2,g3)
    c: Coincident(g3,g0)
    c: Horizontal(g2)
    c: Vertical(g1)
    c: Vertical(g3)
    c: PointOnObject(g1,g-1)
    c: DistanceY(g3,g3) = 50
    c: Symmetric(g0,g0,g-2)
    c: DistanceX(g0,g0) = 44
FEATURE [PartDesign::Pocket] Pocket041
  BaseFeature = -> Pad070
  Length = 5
  Length2 = 100
  Profile = -> Sketch125
  Refine = true
  Reversed = true
  Type = 1
FEATURE [Sketcher::SketchObject] Sketch126
  FullyConstrained = true
  MapMode = 5
  Support = -> [XY_Plane092]
  sketch-geometry (4):
    g0: LineSegment StartX=-6.5 StartY=1 StartZ=0 EndX=6.5 EndY=1 EndZ=0
    g1: LineSegment StartX=6.5 StartY=1 StartZ=0 EndX=6.5 EndY=-8 EndZ=0
    g2: LineSegment StartX=6.5 StartY=-8 StartZ=0 EndX=-6.5 EndY=-8 EndZ=0
    g3: LineSegment StartX=-6.5 StartY=-8 StartZ=0 EndX=-6.5 EndY=1 EndZ=0
  constraints (11):
    c: Coincident(g0,g1)
    c: Coincident(g1,g2)
    c: Coincident(g2,g3)
    c: Coincident(g3,g0)
    c: Horizontal(g0)
    c: Vertical(g1)
    c: Vertical(g3)
    c: DistanceY(g1,g1) = 9
    c: DistanceX(g2,g2) = 13
    c: Symmetric(g2,g1,g-2)
    c: DistanceY(g1,g-1) = 8
FEATURE [PartDesign::Pocket] Pocket042
  BaseFeature = -> Pocket041
  Length = 5
  Length2 = 100
  Profile = -> Sketch126
  Refine = true
  Reversed = true
  Type = 1
FEATURE [Sketcher::SketchObject] Sketch127
  FullyConstrained = true
  MapMode = 5
  Placement = pos=(0,0,0) rot=(1,0,0;1.5708rad)
  Support = -> [XZ_Plane091]
  sketch-geometry (2):
    g0: Circle CenterX=0 CenterY=35 CenterZ=0 NormalX=0 NormalY=0 NormalZ=1 AngleXU=0 Radius=1.75
    g1: Circle CenterX=0 CenterY=10 CenterZ=0 NormalX=0 NormalY=0 NormalZ=1 AngleXU=0 Radius=1.75
  constraints (6):
    c: PointOnObject(g0,g-2)
    c: PointOnObject(g1,g-2)
    c: Diameter(g1) = 3.5
    c: Equal(g1,g0)
    c: DistanceY(g1,g0) = 25
    c: DistanceY(g-1,g1) = 10
FEATURE [PartDesign::Pocket] Pocket043
  BaseFeature = -> Pocket042
  Length = 5
  Length2 = 100
  Profile = -> Sketch127
  Refine = true
  Reversed = true
  Type = 1
FEATURE [Sketcher::SketchObject] Sketch161
  AttachmentOffset = pos=(0,0,17) rot=(0,0,1;0rad)
  FullyConstrained = true
  MapMode = 5
  Placement = pos=(0,0,17) rot=(0,0,1;0rad)
  Support = -> [XY_Plane092]
  sketch-geometry (4):
    g0: LineSegment StartX=-22 StartY=50 StartZ=0 EndX=22 EndY=50 EndZ=0
    g1: LineSegment StartX=22 StartY=50 StartZ=0 EndX=22 EndY=0 EndZ=0
    g2: LineSegment StartX=22 StartY=0 StartZ=0 EndX=-22 EndY=0 EndZ=0
    g3: LineSegment StartX=-22 StartY=0 StartZ=0 EndX=-22 EndY=50 EndZ=0
  constraints (11):
    c: Coincident(g0,g1)
    c: Coincident(g1,g2)
    c: Coincident(g2,g3)
    c: Coincident(g3,g0)
    c: Horizontal(g2)
    c: Vertical(g1)
    c: Vertical(g3)
    c: PointOnObject(g1,g-1)
    c: DistanceY(g3,g3) = 50
    c: Symmetric(g0,g0,g-2)
    c: DistanceX(g0,g0) = 44
FEATURE [PartDesign::Pocket] Pocket060
  BaseFeature = -> Pocket043
  Length = 5
  Length2 = 100
  Profile = -> Sketch161
  Refine = true
  Type = 1
FEATURE [PartDesign::Chamfer] Chamfer
  Angle = 45
  Base = -> Pocket060 [Edge20,Edge16]
  BaseFeature = -> Pocket060
  ChamferType = 1
  FlipDirection = false
  Refine = true
  Size = 18
  Size2 = 47
  SupportTransform = false
FEATURE [PartDesign::Body] Body_10
  Group = -> [LCS_0084,Sketch113,Pad070,Sketch125,Pocket041,Sketch126,Pocket042,Sketch127,Pocket043,Sketch161,Pocket060,Chamfer]
  Origin = -> Origin092
  Tip = -> Chamfer
COMPONENT P29 — recipe-attached ("PCB_BRACK_1V0", modeled in this document).
Construction recipe (the document's own serialized feature program — sketch geometry with constraints, then the solid features built on it; lengths are millimeters unless a unit is written):

FEATURE [PartDesign::CoordinateSystem] LCS_0072
  AttacherType = Attacher::AttachEngine3D
  MapMode = 2
  Support = -> [X_Axis078]
FEATURE [Sketcher::SketchObject] Sketch094
  FullyConstrained = true
  MapMode = 5
  Support = -> [XY_Plane078]
  sketch-geometry (17):
    g0: LineSegment StartX=0 StartY=-35 StartZ=0 EndX=-70 EndY=-35 EndZ=0
    g1: LineSegment StartX=-70 StartY=-35 StartZ=0 EndX=-70 EndY=35 EndZ=0
    g2: LineSegment StartX=-70 StartY=35 StartZ=0 EndX=0 EndY=35 EndZ=0
    g3: LineSegment StartX=0 StartY=35 StartZ=0 EndX=0 EndY=-35 EndZ=0
    g4: Circle CenterX=-65 CenterY=30 CenterZ=0 NormalX=0 NormalY=0 NormalZ=1 AngleXU=0 Radius=1.32
    g5: Circle CenterX=-65 CenterY=-30 CenterZ=0 NormalX=0 NormalY=0 NormalZ=1 AngleXU=0 Radius=1.32
    g6: LineSegment StartX=-65 StartY=30 StartZ=0 EndX=-5 EndY=30 EndZ=0
    g7: LineSegment StartX=-5 StartY=30 StartZ=0 EndX=-5 EndY=-30 EndZ=0
    g8: LineSegment StartX=-5 StartY=-30 StartZ=0 EndX=-65 EndY=-30 EndZ=0
    g9: LineSegment StartX=-65 StartY=-30 StartZ=0 EndX=-65 EndY=30 EndZ=0
    g10: Circle CenterX=-5 CenterY=30 CenterZ=0 NormalX=0 NormalY=0 NormalZ=1 AngleXU=0 Radius=1.32
    g11: Circle CenterX=-5 CenterY=-30 CenterZ=0 NormalX=0 NormalY=0 NormalZ=1 AngleXU=0 Radius=1.32
    g12: Circle CenterX=10 CenterY=-25 CenterZ=0 NormalX=0 NormalY=0 NormalZ=1 AngleXU=0 Radius=2.75
    g13: Circle CenterX=10 CenterY=25 CenterZ=0 NormalX=0 NormalY=0 NormalZ=1 AngleXU=0 Radius=2.75
    g14: LineSegment StartX=0 StartY=35 StartZ=0 EndX=20 EndY=35 EndZ=0
    g15: LineSegment StartX=20 StartY=35 StartZ=0 EndX=20 EndY=-35 EndZ=0
    g16: LineSegment StartX=20 StartY=-35 StartZ=0 EndX=0 EndY=-35 EndZ=0
  constraints (44):
    c: Coincident(g2,g3)
    c: Coincident(g3,g0)
    c: Horizontal(g0)
    c: Horizontal(g2)
    c: Vertical(g1)
    c: PointOnObject(g0,g-2)
    c: Symmetric(g2,g0,g-1)
    c: DistanceY(g3,g3) = 70
    c: Coincident(g6,g7)
    c: Coincident(g7,g8)
    c: Coincident(g8,g9)
    c: Coincident(g9,g6)
    c: Horizontal(g6)
    c: Horizontal(g8)
    c: Coincident(g10,g6)
    c: Coincident(g11,g7)
    c: Diameter(g4) = 2.64
    c: Equal(g4,g10)
    c: Equal(g4,g11)
    c: Equal(g4,g5)
    c: Coincident(g2,g1)
    c: Coincident(g1,g0)
    c: Vertical(g9)
    c: Coincident(g6,g4)
    c: Coincident(g5,g8)
    c: DistanceY(g9,g9) = 60
    c: Symmetric(g10,g11,g-1)
    c: DistanceX(g6,g6) = 60
    c: DistanceX(g0,g0) = 70
    c: DistanceX(g0,g5) = 5
    c: DistanceY(g12,g13) = 50
    c: Diameter(g12) = 5.5
    c: Equal(g12,g13)
    c: DistanceX(g-1,g13) = 10
    c: Vertical(g13,g12)
    c: DistanceY(g0,g12) = 10
    c: Horizontal(g14)
    c: Coincident(g14,g15)
    c: Vertical(g15)
    c: Coincident(g15,g16)
    c: Coincident(g16,g0)
    c: Horizontal(g16)
    c: DistanceX(g13,g14) = 10
    c: Coincident(g14,g2)
FEATURE [PartDesign::Pad] Pad060
  Direction = (1,1,1)
  Length = 5
  Length2 = 100
  Profile = -> Sketch094
  Refine = true
  Reversed = true
  Type = 0
FEATURE [Sketcher::SketchObject] Sketch095
  FullyConstrained = true
  MapMode = 5
  Support = -> [XY_Plane078]
  sketch-geometry (12):
    g0: LineSegment StartX=-65 StartY=30 StartZ=0 EndX=-5 EndY=30 EndZ=0
    g1: LineSegment StartX=-5 StartY=30 StartZ=0 EndX=-5 EndY=-30 EndZ=0
    g2: LineSegment StartX=-5 StartY=-30 StartZ=0 EndX=-65 EndY=-30 EndZ=0
    g3: LineSegment StartX=-65 StartY=-30 StartZ=0 EndX=-65 EndY=30 EndZ=0
    g4: Circle CenterX=-65 CenterY=30 CenterZ=0 NormalX=0 NormalY=0 NormalZ=1 AngleXU=0 Radius=1.32
    g5: Circle CenterX=-65 CenterY=30 CenterZ=0 NormalX=0 NormalY=0 NormalZ=1 AngleXU=0 Radius=3
    g6: Circle CenterX=-5 CenterY=30 CenterZ=0 NormalX=0 NormalY=0 NormalZ=1 AngleXU=0 Radius=1.32
    g7: Circle CenterX=-5 CenterY=30 CenterZ=0 NormalX=0 NormalY=0 NormalZ=1 AngleXU=0 Radius=3
    g8: Circle CenterX=-5 CenterY=-30 CenterZ=0 NormalX=0 NormalY=0 NormalZ=1 AngleXU=0 Radius=1.32
    g9: Circle CenterX=-5 CenterY=-30 CenterZ=0 NormalX=0 NormalY=0 NormalZ=1 AngleXU=0 Radius=3
    g10: Circle CenterX=-65 CenterY=-30 CenterZ=0 NormalX=0 NormalY=0 NormalZ=1 AngleXU=0 Radius=1.32
    g11: Circle CenterX=-65 CenterY=-30 CenterZ=0 NormalX=0 NormalY=0 NormalZ=1 AngleXU=0 Radius=3
  constraints (27):
    c: Coincident(g0,g1)
    c: Coincident(g1,g2)
    c: Coincident(g2,g3)
    c: Coincident(g3,g0)
    c: Horizontal(g0)
    c: Horizontal(g2)
    c: Vertical(g3)
    c: DistanceX(g0,g0) = 60
    c: DistanceY(g3,g3) = 60
    c: Symmetric(g1,g0,g-1)
    c: DistanceX(g1,g-1) = 5
    c: Coincident(g4,g0)
    c: Coincident(g5,g4)
    c: Coincident(g6,g0)
    c: Coincident(g7,g6)
    c: Coincident(g8,g1)
    c: Coincident(g9,g8)
    c: Coincident(g10,g2)
    c: Coincident(g11,g10)
    c: Diameter(g10) = 2.64
    c: Equal(g10,g8)
    c: Equal(g10,g6)
    c: Equal(g10,g4)
    c: Diameter(g7) = 6
    c: Equal(g7,g5)
    c: Equal(g7,g11)
    c: Equal(g7,g9)
FEATURE [PartDesign::Pad] Pad061
  BaseFeature = -> Pad060
  Direction = (1,1,1)
  Length = 4
  Length2 = 100
  Profile = -> Sketch095
  Refine = true
  Type = 0
FEATURE [PartDesign::Body] Body_11
  Group = -> [LCS_0072,Sketch094,Pad060,Sketch095,Pad061]
  Origin = -> Origin078
  Tip = -> Pad061
